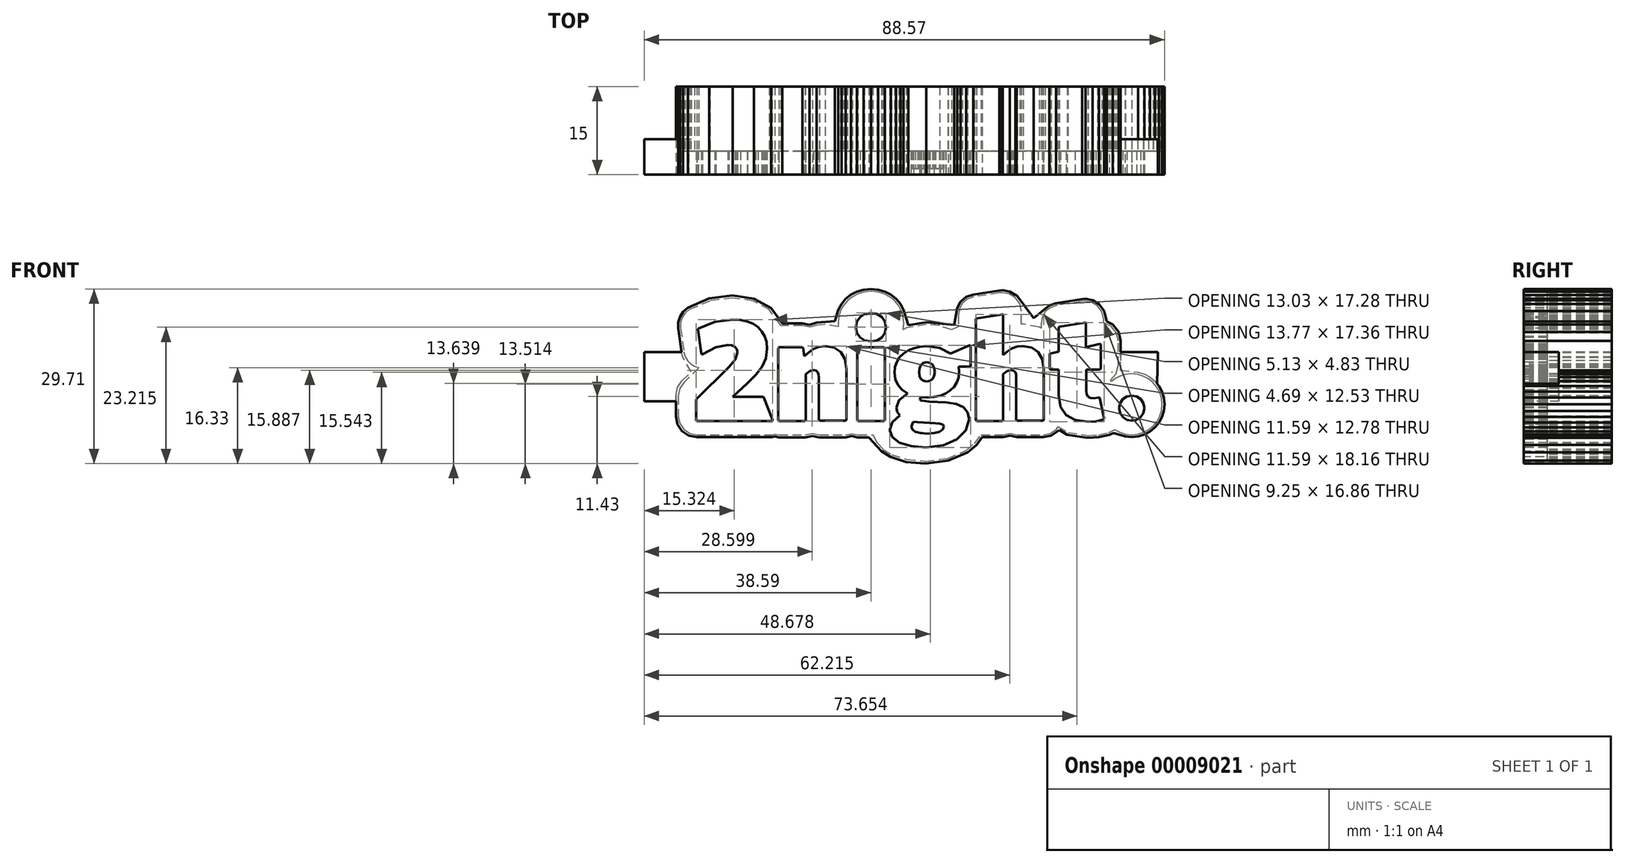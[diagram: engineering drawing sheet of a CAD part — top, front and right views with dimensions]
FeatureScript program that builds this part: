
annotation { "Feature Type Name" : "Feature", "Feature Type Description" : "" }
export const myFeature = defineFeature(function(context is Context, id is Id, definition is map)
    precondition{}
    {
        {
            var Q0;
            Q0=qCreatedBy(makeId("Front.planeOp"),FACE);
            var sketch = newSketch(context, id + "F0", { "sketchPlane" : qUnion([Q0])});
            skLineSegment(sketch, "E0", {"start": v(-31.92, 14.02) * mm, "end": v(-35.81, 13.52) * mm});
            skLineSegment(sketch, "E1", {"start": v(-35.81, 13.52) * mm, "end": v(-39.34, 12) * mm});
            skLineSegment(sketch, "E2", {"start": v(-39.34, 12) * mm, "end": v(-40.05, 11.41) * mm});
            skLineSegment(sketch, "E3", {"start": v(-40.05, 11.41) * mm, "end": v(-40.55, 10.66) * mm});
            skLineSegment(sketch, "E4", {"start": v(-40.55, 10.66) * mm, "end": v(-40.8, 9.8) * mm});
            skLineSegment(sketch, "E5", {"start": v(-40.8, 9.8) * mm, "end": v(-40.8, 8.88) * mm});
            skLineSegment(sketch, "E6", {"start": v(-40.8, 8.88) * mm, "end": v(-40.22, 4.8) * mm});
            skLineSegment(sketch, "E7", {"start": v(-40.22, 4.8) * mm, "end": v(-40.22, 4.75) * mm});
            skLineSegment(sketch, "E8", {"start": v(-40.22, 4.75) * mm, "end": v(-40, 4) * mm});
            skLineSegment(sketch, "E9", {"start": v(-40, 4) * mm, "end": v(-39.61, 3.32) * mm});
            skLineSegment(sketch, "E10", {"start": v(-39.61, 3.32) * mm, "end": v(-39.07, 2.76) * mm});
            skLineSegment(sketch, "E11", {"start": v(-39.07, 2.76) * mm, "end": v(-38.4, 2.35) * mm});
            skLineSegment(sketch, "E12", {"start": v(-38.4, 2.35) * mm, "end": v(-37.68, 2.13) * mm});
            skLineSegment(sketch, "E13", {"start": v(-37.68, 2.13) * mm, "end": v(-40.25, -0.38) * mm});
            skLineSegment(sketch, "E14", {"start": v(-40.25, -0.38) * mm, "end": v(-40.95, -1.42) * mm});
            skLineSegment(sketch, "E15", {"start": v(-40.95, -1.42) * mm, "end": v(-41.19, -2.65) * mm});
            skLineSegment(sketch, "E16", {"start": v(-41.19, -2.65) * mm, "end": v(-41.19, -6.12) * mm});
            skLineSegment(sketch, "E17", {"start": v(-41.19, -6.12) * mm, "end": v(-40.94, -7.35) * mm});
            skLineSegment(sketch, "E18", {"start": v(-40.94, -7.35) * mm, "end": v(-40.26, -8.36) * mm});
            skLineSegment(sketch, "E19", {"start": v(-40.26, -8.36) * mm, "end": v(-39.25, -9.04) * mm});
            skLineSegment(sketch, "E20", {"start": v(-39.25, -9.04) * mm, "end": v(-38.01, -9.3) * mm});
            skLineSegment(sketch, "E21", {"start": v(-38.01, -9.3) * mm, "end": v(-25.24, -9.3) * mm});
            skLineSegment(sketch, "E22", {"start": v(-25.24, -9.3) * mm, "end": v(-23.8, -8.94) * mm});
            skLineSegment(sketch, "E23", {"start": v(-23.8, -8.94) * mm, "end": v(-22.65, -7.97) * mm});
            skLineSegment(sketch, "E24", {"start": v(-22.65, -7.97) * mm, "end": v(-22.65, -7.92) * mm});
            skLineSegment(sketch, "E25", {"start": v(-22.65, -7.92) * mm, "end": v(-22.12, -6.5) * mm});
            skLineSegment(sketch, "E26", {"start": v(-22.12, -6.5) * mm, "end": v(-22.32, -5) * mm});
            skLineSegment(sketch, "E27", {"start": v(-22.32, -5) * mm, "end": v(-23.8, -1.16) * mm});
            skLineSegment(sketch, "E28", {"start": v(-23.8, -1.16) * mm, "end": v(-24.31, -0.3) * mm});
            skLineSegment(sketch, "E29", {"start": v(-24.31, -0.3) * mm, "end": v(-25.05, 0.36) * mm});
            skLineSegment(sketch, "E30", {"start": v(-25.05, 0.36) * mm, "end": v(-24.26, 1.54) * mm});
            skLineSegment(sketch, "E31", {"start": v(-24.26, 1.54) * mm, "end": v(-23.63, 2.87) * mm});
            skLineSegment(sketch, "E32", {"start": v(-23.63, 2.87) * mm, "end": v(-23.21, 4.36) * mm});
            skLineSegment(sketch, "E33", {"start": v(-23.21, 4.36) * mm, "end": v(-23.06, 6.04) * mm});
            skLineSegment(sketch, "E34", {"start": v(-23.06, 6.04) * mm, "end": v(-23.74, 9.38) * mm});
            skLineSegment(sketch, "E35", {"start": v(-23.74, 9.38) * mm, "end": v(-25.68, 12) * mm});
            skLineSegment(sketch, "E36", {"start": v(-25.68, 12) * mm, "end": v(-28.44, 13.5) * mm});
            skLineSegment(sketch, "E37", {"start": v(-28.44, 13.5) * mm, "end": v(-31.92, 14.02) * mm});
            skLineSegment(sketch, "E38", {"start": v(-16.2, 9.52) * mm, "end": v(-17.59, 9.39) * mm});
            skLineSegment(sketch, "E39", {"start": v(-17.59, 9.39) * mm, "end": v(-18.81, 9.02) * mm});
            skLineSegment(sketch, "E40", {"start": v(-18.81, 9.02) * mm, "end": v(-20.08, 9.27) * mm});
            skLineSegment(sketch, "E41", {"start": v(-20.08, 9.27) * mm, "end": v(-24.03, 9.27) * mm});
            skLineSegment(sketch, "E42", {"start": v(-24.03, 9.27) * mm, "end": v(-25.26, 9.02) * mm});
            skLineSegment(sketch, "E43", {"start": v(-25.26, 9.02) * mm, "end": v(-26.27, 8.35) * mm});
            skLineSegment(sketch, "E44", {"start": v(-26.27, 8.35) * mm, "end": v(-26.95, 7.34) * mm});
            skLineSegment(sketch, "E45", {"start": v(-26.95, 7.34) * mm, "end": v(-27.2, 6.1) * mm});
            skLineSegment(sketch, "E46", {"start": v(-27.2, 6.1) * mm, "end": v(-27.2, -6.15) * mm});
            skLineSegment(sketch, "E47", {"start": v(-27.2, -6.15) * mm, "end": v(-26.95, -7.38) * mm});
            skLineSegment(sketch, "E48", {"start": v(-26.95, -7.38) * mm, "end": v(-26.28, -8.39) * mm});
            skLineSegment(sketch, "E49", {"start": v(-26.28, -8.39) * mm, "end": v(-25.27, -9.07) * mm});
            skLineSegment(sketch, "E50", {"start": v(-25.27, -9.07) * mm, "end": v(-24.03, -9.32) * mm});
            skLineSegment(sketch, "E51", {"start": v(-24.03, -9.32) * mm, "end": v(-19.61, -9.32) * mm});
            skLineSegment(sketch, "E52", {"start": v(-19.61, -9.32) * mm, "end": v(-18.37, -9.07) * mm});
            skLineSegment(sketch, "E53", {"start": v(-18.37, -9.07) * mm, "end": v(-17.13, -9.32) * mm});
            skLineSegment(sketch, "E54", {"start": v(-17.13, -9.32) * mm, "end": v(-12.72, -9.32) * mm});
            skLineSegment(sketch, "E55", {"start": v(-12.72, -9.32) * mm, "end": v(-11.49, -9.07) * mm});
            skLineSegment(sketch, "E56", {"start": v(-11.49, -9.07) * mm, "end": v(-10.48, -8.4) * mm});
            skLineSegment(sketch, "E57", {"start": v(-10.48, -8.4) * mm, "end": v(-9.8, -7.39) * mm});
            skLineSegment(sketch, "E58", {"start": v(-9.8, -7.39) * mm, "end": v(-9.55, -6.15) * mm});
            skLineSegment(sketch, "E59", {"start": v(-9.55, -6.15) * mm, "end": v(-9.55, 2.49) * mm});
            skLineSegment(sketch, "E60", {"start": v(-9.55, 2.49) * mm, "end": v(-10.03, 5.39) * mm});
            skLineSegment(sketch, "E61", {"start": v(-10.03, 5.39) * mm, "end": v(-11.37, 7.6) * mm});
            skLineSegment(sketch, "E62", {"start": v(-11.37, 7.6) * mm, "end": v(-13.46, 9.02) * mm});
            skLineSegment(sketch, "E63", {"start": v(-13.46, 9.02) * mm, "end": v(-16.2, 9.52) * mm});
            skLineSegment(sketch, "E64", {"start": v(-8.39, 15.12) * mm, "end": v(-9.55, 15.01) * mm});
            skLineSegment(sketch, "E65", {"start": v(-9.55, 15.01) * mm, "end": v(-10.61, 14.7) * mm});
            skLineSegment(sketch, "E66", {"start": v(-10.61, 14.7) * mm, "end": v(-11.57, 14.21) * mm});
            skLineSegment(sketch, "E67", {"start": v(-11.57, 14.21) * mm, "end": v(-12.39, 13.56) * mm});
            skLineSegment(sketch, "E68", {"start": v(-12.39, 13.56) * mm, "end": v(-13.06, 12.76) * mm});
            skLineSegment(sketch, "E69", {"start": v(-13.06, 12.76) * mm, "end": v(-13.56, 11.83) * mm});
            skLineSegment(sketch, "E70", {"start": v(-13.56, 11.83) * mm, "end": v(-13.88, 10.79) * mm});
            skLineSegment(sketch, "E71", {"start": v(-13.88, 10.79) * mm, "end": v(-13.99, 9.66) * mm});
            skLineSegment(sketch, "E72", {"start": v(-13.99, 9.66) * mm, "end": v(-13.88, 8.54) * mm});
            skLineSegment(sketch, "E73", {"start": v(-13.88, 8.54) * mm, "end": v(-13.56, 7.5) * mm});
            skLineSegment(sketch, "E74", {"start": v(-13.56, 7.5) * mm, "end": v(-13.06, 6.58) * mm});
            skLineSegment(sketch, "E75", {"start": v(-13.06, 6.58) * mm, "end": v(-12.39, 5.78) * mm});
            skLineSegment(sketch, "E76", {"start": v(-12.39, 5.78) * mm, "end": v(-11.57, 5.13) * mm});
            skLineSegment(sketch, "E77", {"start": v(-11.57, 5.13) * mm, "end": v(-10.61, 4.64) * mm});
            skLineSegment(sketch, "E78", {"start": v(-10.61, 4.64) * mm, "end": v(-9.55, 4.33) * mm});
            skLineSegment(sketch, "E79", {"start": v(-9.55, 4.33) * mm, "end": v(-8.39, 4.22) * mm});
            skLineSegment(sketch, "E80", {"start": v(-8.39, 4.22) * mm, "end": v(-7.23, 4.33) * mm});
            skLineSegment(sketch, "E81", {"start": v(-7.23, 4.33) * mm, "end": v(-6.16, 4.64) * mm});
            skLineSegment(sketch, "E82", {"start": v(-6.16, 4.64) * mm, "end": v(-5.2, 5.13) * mm});
            skLineSegment(sketch, "E83", {"start": v(-5.2, 5.13) * mm, "end": v(-4.39, 5.78) * mm});
            skLineSegment(sketch, "E84", {"start": v(-4.39, 5.78) * mm, "end": v(-3.71, 6.58) * mm});
            skLineSegment(sketch, "E85", {"start": v(-3.71, 6.58) * mm, "end": v(-3.21, 7.5) * mm});
            skLineSegment(sketch, "E86", {"start": v(-3.21, 7.5) * mm, "end": v(-2.9, 8.54) * mm});
            skLineSegment(sketch, "E87", {"start": v(-2.9, 8.54) * mm, "end": v(-2.79, 9.66) * mm});
            skLineSegment(sketch, "E88", {"start": v(-2.79, 9.66) * mm, "end": v(-2.89, 10.79) * mm});
            skLineSegment(sketch, "E89", {"start": v(-2.89, 10.79) * mm, "end": v(-3.2, 11.83) * mm});
            skLineSegment(sketch, "E90", {"start": v(-3.2, 11.83) * mm, "end": v(-3.7, 12.76) * mm});
            skLineSegment(sketch, "E91", {"start": v(-3.7, 12.76) * mm, "end": v(-4.38, 13.56) * mm});
            skLineSegment(sketch, "E92", {"start": v(-4.38, 13.56) * mm, "end": v(-5.2, 14.21) * mm});
            skLineSegment(sketch, "E93", {"start": v(-5.2, 14.21) * mm, "end": v(-6.16, 14.7) * mm});
            skLineSegment(sketch, "E94", {"start": v(-6.16, 14.7) * mm, "end": v(-7.23, 15.01) * mm});
            skLineSegment(sketch, "E95", {"start": v(-7.23, 15.01) * mm, "end": v(-8.39, 15.12) * mm});
            skLineSegment(sketch, "E96", {"start": v(-6.18, 9.27) * mm, "end": v(-10.6, 9.27) * mm});
            skLineSegment(sketch, "E97", {"start": v(-10.6, 9.27) * mm, "end": v(-11.82, 9.02) * mm});
            skLineSegment(sketch, "E98", {"start": v(-11.82, 9.02) * mm, "end": v(-12.83, 8.35) * mm});
            skLineSegment(sketch, "E99", {"start": v(-12.83, 8.35) * mm, "end": v(-13.52, 7.34) * mm});
            skLineSegment(sketch, "E100", {"start": v(-13.52, 7.34) * mm, "end": v(-13.77, 6.1) * mm});
            skLineSegment(sketch, "E101", {"start": v(-13.77, 6.1) * mm, "end": v(-13.77, -6.15) * mm});
            skLineSegment(sketch, "E102", {"start": v(-13.77, -6.15) * mm, "end": v(-13.52, -7.38) * mm});
            skLineSegment(sketch, "E103", {"start": v(-13.52, -7.38) * mm, "end": v(-12.84, -8.39) * mm});
            skLineSegment(sketch, "E104", {"start": v(-12.84, -8.39) * mm, "end": v(-11.83, -9.07) * mm});
            skLineSegment(sketch, "E105", {"start": v(-11.83, -9.07) * mm, "end": v(-10.6, -9.32) * mm});
            skLineSegment(sketch, "E106", {"start": v(-10.6, -9.32) * mm, "end": v(-6.18, -9.32) * mm});
            skLineSegment(sketch, "E107", {"start": v(-6.18, -9.32) * mm, "end": v(-4.95, -9.07) * mm});
            skLineSegment(sketch, "E108", {"start": v(-4.95, -9.07) * mm, "end": v(-3.94, -8.4) * mm});
            skLineSegment(sketch, "E109", {"start": v(-3.94, -8.4) * mm, "end": v(-3.26, -7.39) * mm});
            skLineSegment(sketch, "E110", {"start": v(-3.26, -7.39) * mm, "end": v(-3, -6.15) * mm});
            skLineSegment(sketch, "E111", {"start": v(-3, -6.15) * mm, "end": v(-3, 6.13) * mm});
            skLineSegment(sketch, "E112", {"start": v(-3, 6.13) * mm, "end": v(-3.26, 7.35) * mm});
            skLineSegment(sketch, "E113", {"start": v(-3.26, 7.35) * mm, "end": v(-3.94, 8.35) * mm});
            skLineSegment(sketch, "E114", {"start": v(-3.94, 8.35) * mm, "end": v(-4.95, 9.03) * mm});
            skLineSegment(sketch, "E115", {"start": v(-4.95, 9.03) * mm, "end": v(-6.18, 9.27) * mm});
            skLineSegment(sketch, "E116", {"start": v(8.39, 9.63) * mm, "end": v(7.17, 9.38) * mm});
            skLineSegment(sketch, "E117", {"start": v(7.17, 9.38) * mm, "end": v(5.32, 8.6) * mm});
            skLineSegment(sketch, "E118", {"start": v(5.32, 8.6) * mm, "end": v(3.3, 9.27) * mm});
            skLineSegment(sketch, "E119", {"start": v(3.3, 9.27) * mm, "end": v(1.05, 9.5) * mm});
            skLineSegment(sketch, "E120", {"start": v(1.05, 9.5) * mm, "end": v(-2.35, 8.93) * mm});
            skLineSegment(sketch, "E121", {"start": v(-2.35, 8.93) * mm, "end": v(-5.04, 7.36) * mm});
            skLineSegment(sketch, "E122", {"start": v(-5.04, 7.36) * mm, "end": v(-6.81, 4.97) * mm});
            skLineSegment(sketch, "E123", {"start": v(-6.81, 4.97) * mm, "end": v(-7.45, 1.93) * mm});
            skLineSegment(sketch, "E124", {"start": v(-7.45, 1.93) * mm, "end": v(-7.2, 0.06) * mm});
            skLineSegment(sketch, "E125", {"start": v(-7.2, 0.06) * mm, "end": v(-6.51, -1.6) * mm});
            skLineSegment(sketch, "E126", {"start": v(-6.51, -1.6) * mm, "end": v(-7, -2.85) * mm});
            skLineSegment(sketch, "E127", {"start": v(-7, -2.85) * mm, "end": v(-7.14, -3.97) * mm});
            skLineSegment(sketch, "E128", {"start": v(-7.14, -3.97) * mm, "end": v(-7.12, -4.44) * mm});
            skLineSegment(sketch, "E129", {"start": v(-7.12, -4.44) * mm, "end": v(-7.99, -6) * mm});
            skLineSegment(sketch, "E130", {"start": v(-7.99, -6) * mm, "end": v(-8.28, -7.8) * mm});
            skLineSegment(sketch, "E131", {"start": v(-8.28, -7.8) * mm, "end": v(-8.05, -9.3) * mm});
            skLineSegment(sketch, "E132", {"start": v(-8.05, -9.3) * mm, "end": v(-7.39, -10.63) * mm});
            skLineSegment(sketch, "E133", {"start": v(-7.39, -10.63) * mm, "end": v(-6.32, -11.77) * mm});
            skLineSegment(sketch, "E134", {"start": v(-6.32, -11.77) * mm, "end": v(-4.88, -12.69) * mm});
            skLineSegment(sketch, "E135", {"start": v(-4.88, -12.69) * mm, "end": v(-2.3, -13.52) * mm});
            skLineSegment(sketch, "E136", {"start": v(-2.3, -13.52) * mm, "end": v(0.88, -13.8) * mm});
            skLineSegment(sketch, "E137", {"start": v(0.88, -13.8) * mm, "end": v(4.69, -13.32) * mm});
            skLineSegment(sketch, "E138", {"start": v(4.69, -13.32) * mm, "end": v(7.83, -11.94) * mm});
            skLineSegment(sketch, "E139", {"start": v(7.83, -11.94) * mm, "end": v(9.29, -10.73) * mm});
            skLineSegment(sketch, "E140", {"start": v(9.29, -10.73) * mm, "end": v(10.36, -9.3) * mm});
            skLineSegment(sketch, "E141", {"start": v(10.36, -9.3) * mm, "end": v(11.03, -7.68) * mm});
            skLineSegment(sketch, "E142", {"start": v(11.03, -7.68) * mm, "end": v(11.25, -5.93) * mm});
            skLineSegment(sketch, "E143", {"start": v(11.25, -5.93) * mm, "end": v(11.17, -4.91) * mm});
            skLineSegment(sketch, "E144", {"start": v(11.17, -4.91) * mm, "end": v(10.83, -3.68) * mm});
            skLineSegment(sketch, "E145", {"start": v(10.83, -3.68) * mm, "end": v(10.07, -2.4) * mm});
            skLineSegment(sketch, "E146", {"start": v(10.07, -2.4) * mm, "end": v(8.74, -1.24) * mm});
            skLineSegment(sketch, "E147", {"start": v(8.74, -1.24) * mm, "end": v(9.3, 0.14) * mm});
            skLineSegment(sketch, "E148", {"start": v(9.3, 0.14) * mm, "end": v(10.6, 0.91) * mm});
            skLineSegment(sketch, "E149", {"start": v(10.6, 0.91) * mm, "end": v(10.65, 0.97) * mm});
            skLineSegment(sketch, "E150", {"start": v(10.65, 0.97) * mm, "end": v(11.3, 1.98) * mm});
            skLineSegment(sketch, "E151", {"start": v(11.3, 1.98) * mm, "end": v(11.53, 3.15) * mm});
            skLineSegment(sketch, "E152", {"start": v(11.53, 3.15) * mm, "end": v(11.5, 6.49) * mm});
            skLineSegment(sketch, "E153", {"start": v(11.5, 6.49) * mm, "end": v(11.13, 7.96) * mm});
            skLineSegment(sketch, "E154", {"start": v(11.13, 7.96) * mm, "end": v(10.12, 9.08) * mm});
            skLineSegment(sketch, "E155", {"start": v(10.12, 9.08) * mm, "end": v(9.3, 9.49) * mm});
            skLineSegment(sketch, "E156", {"start": v(9.3, 9.49) * mm, "end": v(8.39, 9.63) * mm});
            skLineSegment(sketch, "E157", {"start": v(14.01, 14.9) * mm, "end": v(13.63, 14.87) * mm});
            skLineSegment(sketch, "E158", {"start": v(13.63, 14.87) * mm, "end": v(13.52, 14.87) * mm});
            skLineSegment(sketch, "E159", {"start": v(13.52, 14.87) * mm, "end": v(9.1, 14.18) * mm});
            skLineSegment(sketch, "E160", {"start": v(9.1, 14.18) * mm, "end": v(8.04, 13.8) * mm});
            skLineSegment(sketch, "E161", {"start": v(8.04, 13.8) * mm, "end": v(7.2, 13.11) * mm});
            skLineSegment(sketch, "E162", {"start": v(7.2, 13.11) * mm, "end": v(6.65, 12.17) * mm});
            skLineSegment(sketch, "E163", {"start": v(6.65, 12.17) * mm, "end": v(6.45, 11.06) * mm});
            skLineSegment(sketch, "E164", {"start": v(6.45, 11.06) * mm, "end": v(6.45, -6.12) * mm});
            skLineSegment(sketch, "E165", {"start": v(6.45, -6.12) * mm, "end": v(6.7, -7.35) * mm});
            skLineSegment(sketch, "E166", {"start": v(6.7, -7.35) * mm, "end": v(7.38, -8.36) * mm});
            skLineSegment(sketch, "E167", {"start": v(7.38, -8.36) * mm, "end": v(8.39, -9.04) * mm});
            skLineSegment(sketch, "E168", {"start": v(8.39, -9.04) * mm, "end": v(9.63, -9.3) * mm});
            skLineSegment(sketch, "E169", {"start": v(9.63, -9.3) * mm, "end": v(14.04, -9.3) * mm});
            skLineSegment(sketch, "E170", {"start": v(14.04, -9.3) * mm, "end": v(15.28, -9.05) * mm});
            skLineSegment(sketch, "E171", {"start": v(15.28, -9.05) * mm, "end": v(16.52, -9.3) * mm});
            skLineSegment(sketch, "E172", {"start": v(16.52, -9.3) * mm, "end": v(20.94, -9.3) * mm});
            skLineSegment(sketch, "E173", {"start": v(20.94, -9.3) * mm, "end": v(22.17, -9.05) * mm});
            skLineSegment(sketch, "E174", {"start": v(22.17, -9.05) * mm, "end": v(23.17, -8.37) * mm});
            skLineSegment(sketch, "E175", {"start": v(23.17, -8.37) * mm, "end": v(23.86, -7.36) * mm});
            skLineSegment(sketch, "E176", {"start": v(23.86, -7.36) * mm, "end": v(24.1, -6.12) * mm});
            skLineSegment(sketch, "E177", {"start": v(24.1, -6.12) * mm, "end": v(24.1, 2.51) * mm});
            skLineSegment(sketch, "E178", {"start": v(24.1, 2.51) * mm, "end": v(23.64, 5.42) * mm});
            skLineSegment(sketch, "E179", {"start": v(23.64, 5.42) * mm, "end": v(22.31, 7.63) * mm});
            skLineSegment(sketch, "E180", {"start": v(22.31, 7.63) * mm, "end": v(20.23, 9.05) * mm});
            skLineSegment(sketch, "E181", {"start": v(20.23, 9.05) * mm, "end": v(17.52, 9.55) * mm});
            skLineSegment(sketch, "E182", {"start": v(17.52, 9.55) * mm, "end": v(17.24, 9.55) * mm});
            skLineSegment(sketch, "E183", {"start": v(17.24, 9.55) * mm, "end": v(17.24, 11.75) * mm});
            skLineSegment(sketch, "E184", {"start": v(17.24, 11.75) * mm, "end": v(16.96, 13.05) * mm});
            skLineSegment(sketch, "E185", {"start": v(16.96, 13.05) * mm, "end": v(16.17, 14.13) * mm});
            skLineSegment(sketch, "E186", {"start": v(16.17, 14.13) * mm, "end": v(16.08, 14.13) * mm});
            skLineSegment(sketch, "E187", {"start": v(16.08, 14.13) * mm, "end": v(16.06, 14.15) * mm});
            skLineSegment(sketch, "E188", {"start": v(16.06, 14.15) * mm, "end": v(15.1, 14.7) * mm});
            skLineSegment(sketch, "E189", {"start": v(15.1, 14.7) * mm, "end": v(14.01, 14.9) * mm});
            skLineSegment(sketch, "E190", {"start": v(28.08, 13.46) * mm, "end": v(27.59, 13.44) * mm});
            skLineSegment(sketch, "E191", {"start": v(27.59, 13.44) * mm, "end": v(23.23, 12.75) * mm});
            skLineSegment(sketch, "E192", {"start": v(23.23, 12.75) * mm, "end": v(22.16, 12.38) * mm});
            skLineSegment(sketch, "E193", {"start": v(22.16, 12.38) * mm, "end": v(21.3, 11.68) * mm});
            skLineSegment(sketch, "E194", {"start": v(21.3, 11.68) * mm, "end": v(20.75, 10.75) * mm});
            skLineSegment(sketch, "E195", {"start": v(20.75, 10.75) * mm, "end": v(20.55, 9.63) * mm});
            skLineSegment(sketch, "E196", {"start": v(20.55, 9.63) * mm, "end": v(20.55, 7.78) * mm});
            skLineSegment(sketch, "E197", {"start": v(20.55, 7.78) * mm, "end": v(19.91, 7.29) * mm});
            skLineSegment(sketch, "E198", {"start": v(19.91, 7.29) * mm, "end": v(19.43, 6.65) * mm});
            skLineSegment(sketch, "E199", {"start": v(19.43, 6.65) * mm, "end": v(19.12, 5.9) * mm});
            skLineSegment(sketch, "E200", {"start": v(19.12, 5.9) * mm, "end": v(19, 5.08) * mm});
            skLineSegment(sketch, "E201", {"start": v(19, 5.08) * mm, "end": v(19, 2.6) * mm});
            skLineSegment(sketch, "E202", {"start": v(19, 2.6) * mm, "end": v(19.12, 1.76) * mm});
            skLineSegment(sketch, "E203", {"start": v(19.12, 1.76) * mm, "end": v(19.43, 1.02) * mm});
            skLineSegment(sketch, "E204", {"start": v(19.43, 1.02) * mm, "end": v(19.91, 0.38) * mm});
            skLineSegment(sketch, "E205", {"start": v(19.91, 0.38) * mm, "end": v(20.55, -0.1) * mm});
            skLineSegment(sketch, "E206", {"start": v(20.55, -0.1) * mm, "end": v(20.55, -1.85) * mm});
            skLineSegment(sketch, "E207", {"start": v(20.55, -1.85) * mm, "end": v(21.1, -5.03) * mm});
            skLineSegment(sketch, "E208", {"start": v(21.1, -5.03) * mm, "end": v(22.67, -7.42) * mm});
            skLineSegment(sketch, "E209", {"start": v(22.67, -7.42) * mm, "end": v(25.18, -8.91) * mm});
            skLineSegment(sketch, "E210", {"start": v(25.18, -8.91) * mm, "end": v(28.55, -9.43) * mm});
            skLineSegment(sketch, "E211", {"start": v(28.55, -9.43) * mm, "end": v(30.34, -9.32) * mm});
            skLineSegment(sketch, "E212", {"start": v(30.34, -9.32) * mm, "end": v(32.06, -8.94) * mm});
            skLineSegment(sketch, "E213", {"start": v(32.06, -8.94) * mm, "end": v(33.1, -8.39) * mm});
            skLineSegment(sketch, "E214", {"start": v(33.1, -8.39) * mm, "end": v(33.87, -7.51) * mm});
            skLineSegment(sketch, "E215", {"start": v(33.87, -7.51) * mm, "end": v(34.27, -6.43) * mm});
            skLineSegment(sketch, "E216", {"start": v(34.27, -6.43) * mm, "end": v(34.24, -5.24) * mm});
            skLineSegment(sketch, "E217", {"start": v(34.24, -5.24) * mm, "end": v(33.46, -1.74) * mm});
            skLineSegment(sketch, "E218", {"start": v(33.46, -1.74) * mm, "end": v(33.07, -0.77) * mm});
            skLineSegment(sketch, "E219", {"start": v(33.07, -0.77) * mm, "end": v(32.39, 0) * mm});
            skLineSegment(sketch, "E220", {"start": v(32.39, 0) * mm, "end": v(33.35, 1.1) * mm});
            skLineSegment(sketch, "E221", {"start": v(33.35, 1.1) * mm, "end": v(33.71, 2.54) * mm});
            skLineSegment(sketch, "E222", {"start": v(33.71, 2.54) * mm, "end": v(33.74, 6.68) * mm});
            skLineSegment(sketch, "E223", {"start": v(33.74, 6.68) * mm, "end": v(33.42, 8.05) * mm});
            skLineSegment(sketch, "E224", {"start": v(33.42, 8.05) * mm, "end": v(32.52, 9.16) * mm});
            skLineSegment(sketch, "E225", {"start": v(32.52, 9.16) * mm, "end": v(31.26, 9.77) * mm});
            skLineSegment(sketch, "E226", {"start": v(31.26, 9.77) * mm, "end": v(31.26, 10.3) * mm});
            skLineSegment(sketch, "E227", {"start": v(31.26, 10.3) * mm, "end": v(30.96, 11.63) * mm});
            skLineSegment(sketch, "E228", {"start": v(30.96, 11.63) * mm, "end": v(30.15, 12.7) * mm});
            skLineSegment(sketch, "E229", {"start": v(30.15, 12.7) * mm, "end": v(29.19, 13.26) * mm});
            skLineSegment(sketch, "E230", {"start": v(29.19, 13.26) * mm, "end": v(28.08, 13.46) * mm});
            skLineSegment(sketch, "E231", {"start": v(36, 1.08) * mm, "end": v(34.95, 0.97) * mm});
            skLineSegment(sketch, "E232", {"start": v(34.95, 0.97) * mm, "end": v(33.98, 0.67) * mm});
            skLineSegment(sketch, "E233", {"start": v(33.98, 0.67) * mm, "end": v(33.1, 0.2) * mm});
            skLineSegment(sketch, "E234", {"start": v(33.1, 0.2) * mm, "end": v(32.33, -0.44) * mm});
            skLineSegment(sketch, "E235", {"start": v(32.33, -0.44) * mm, "end": v(31.7, -1.2) * mm});
            skLineSegment(sketch, "E236", {"start": v(31.7, -1.2) * mm, "end": v(31.22, -2.09) * mm});
            skLineSegment(sketch, "E237", {"start": v(31.22, -2.09) * mm, "end": v(30.92, -3.06) * mm});
            skLineSegment(sketch, "E238", {"start": v(30.92, -3.06) * mm, "end": v(30.81, -4.1) * mm});
            skLineSegment(sketch, "E239", {"start": v(30.81, -4.1) * mm, "end": v(30.92, -5.15) * mm});
            skLineSegment(sketch, "E240", {"start": v(30.92, -5.15) * mm, "end": v(31.22, -6.13) * mm});
            skLineSegment(sketch, "E241", {"start": v(31.22, -6.13) * mm, "end": v(31.7, -7) * mm});
            skLineSegment(sketch, "E242", {"start": v(31.7, -7) * mm, "end": v(32.33, -7.78) * mm});
            skLineSegment(sketch, "E243", {"start": v(32.33, -7.78) * mm, "end": v(33.1, -8.4) * mm});
            skLineSegment(sketch, "E244", {"start": v(33.1, -8.4) * mm, "end": v(33.98, -8.89) * mm});
            skLineSegment(sketch, "E245", {"start": v(33.98, -8.89) * mm, "end": v(34.95, -9.19) * mm});
            skLineSegment(sketch, "E246", {"start": v(34.95, -9.19) * mm, "end": v(36, -9.3) * mm});
            skLineSegment(sketch, "E247", {"start": v(36, -9.3) * mm, "end": v(37.05, -9.19) * mm});
            skLineSegment(sketch, "E248", {"start": v(37.05, -9.19) * mm, "end": v(38.02, -8.89) * mm});
            skLineSegment(sketch, "E249", {"start": v(38.02, -8.89) * mm, "end": v(38.9, -8.4) * mm});
            skLineSegment(sketch, "E250", {"start": v(38.9, -8.4) * mm, "end": v(39.67, -7.78) * mm});
            skLineSegment(sketch, "E251", {"start": v(39.67, -7.78) * mm, "end": v(40.3, -7) * mm});
            skLineSegment(sketch, "E252", {"start": v(40.3, -7) * mm, "end": v(40.78, -6.13) * mm});
            skLineSegment(sketch, "E253", {"start": v(40.78, -6.13) * mm, "end": v(41.08, -5.15) * mm});
            skLineSegment(sketch, "E254", {"start": v(41.08, -5.15) * mm, "end": v(41.19, -4.1) * mm});
            skLineSegment(sketch, "E255", {"start": v(41.19, -4.1) * mm, "end": v(41.08, -3.06) * mm});
            skLineSegment(sketch, "E256", {"start": v(41.08, -3.06) * mm, "end": v(40.78, -2.09) * mm});
            skLineSegment(sketch, "E257", {"start": v(40.78, -2.09) * mm, "end": v(40.3, -1.2) * mm});
            skLineSegment(sketch, "E258", {"start": v(40.3, -1.2) * mm, "end": v(39.66, -0.44) * mm});
            skLineSegment(sketch, "E259", {"start": v(39.66, -0.44) * mm, "end": v(38.89, 0.2) * mm});
            skLineSegment(sketch, "E260", {"start": v(38.89, 0.2) * mm, "end": v(38, 0.67) * mm});
            skLineSegment(sketch, "E261", {"start": v(38, 0.67) * mm, "end": v(37.04, 0.97) * mm});
            skLineSegment(sketch, "E262", {"start": v(37.04, 0.97) * mm, "end": v(36, 1.08) * mm});
            skSolve(sketch);
        }
        {
            var Q0;
            {var subQ12=sQuery(id+"F0.wireOp",EDGE,"E86");Q0=makeQuery(id+"F0.imprint","IMPRINT",FACE,{"disambiguationData":[TD([[makeQuery(id+"F0.imprint","IMPRINT",EDGE,{"derivedFrom":subQ12}),-1.0]])]});}
            var Q1;
            Q1=makeQuery(id+"F0.imprint","IMPRINT",FACE,{"disambiguationData":[TD([[makeQuery(id+"F0.imprint","IMPRINT",EDGE,{"derivedFrom":sQuery(id+"F0.wireOp",EDGE,"E0")}),1.0]])]});
            var Q2;
            {var subQ3=sQuery(id+"F0.wireOp",EDGE,"E214");Q2=makeQuery(id+"F0.imprint","IMPRINT",FACE,{"disambiguationData":[TD([[makeQuery(id+"F0.imprint","IMPRINT",EDGE,{"derivedFrom":subQ3}),-1.0]])]});}
            var Q3;
            {var subQ3=sQuery(id+"F0.wireOp",EDGE,"E23");Q3=makeQuery(id+"F0.imprint","IMPRINT",FACE,{"disambiguationData":[TD([[makeQuery(id+"F0.imprint","IMPRINT",EDGE,{"derivedFrom":subQ3}),1.0]])]});}
            var Q4;
            {var subQ9=sQuery(id+"F0.wireOp",EDGE,"E116");Q4=makeQuery(id+"F0.imprint","IMPRINT",FACE,{"disambiguationData":[TD([[makeQuery(id+"F0.imprint","IMPRINT",EDGE,{"derivedFrom":subQ9}),-1.0]])]});}
            var Q5;
            {var subQ4=sQuery(id+"F0.wireOp",EDGE,"E116");Q5=makeQuery(id+"F0.imprint","IMPRINT",FACE,{"disambiguationData":[TD([[makeQuery(id+"F0.imprint","IMPRINT",EDGE,{"derivedFrom":subQ4}),1.0]])]});}
            var Q6;
            {var subQ17=sQuery(id+"F0.wireOp",EDGE,"E176");Q6=makeQuery(id+"F0.imprint","IMPRINT",FACE,{"disambiguationData":[TD([[makeQuery(id+"F0.imprint","IMPRINT",EDGE,{"derivedFrom":subQ17}),-1.0]])]});}
            var Q7;
            {var subQ9=sQuery(id+"F0.wireOp",EDGE,"E176");Q7=makeQuery(id+"F0.imprint","IMPRINT",FACE,{"disambiguationData":[TD([[makeQuery(id+"F0.imprint","IMPRINT",EDGE,{"derivedFrom":subQ9}),1.0]])]});}
            var Q8;
            {var subQ17=sQuery(id+"F0.wireOp",EDGE,"E23");Q8=makeQuery(id+"F0.imprint","IMPRINT",FACE,{"disambiguationData":[TD([[makeQuery(id+"F0.imprint","IMPRINT",EDGE,{"derivedFrom":subQ17}),-1.0]])]});}
            var Q9;
            {var subQ14=sQuery(id+"F0.wireOp",EDGE,"E56");Q9=makeQuery(id+"F0.imprint","IMPRINT",FACE,{"disambiguationData":[TD([[makeQuery(id+"F0.imprint","IMPRINT",EDGE,{"derivedFrom":subQ14}),1.0]])]});}
            var Q10;
            {var subQ12=sQuery(id+"F0.wireOp",EDGE,"E82");Q10=makeQuery(id+"F0.imprint","IMPRINT",FACE,{"disambiguationData":[TD([[makeQuery(id+"F0.imprint","IMPRINT",EDGE,{"derivedFrom":subQ12}),-1.0]])]});}
            var Q11;
            {var subQ18=sQuery(id+"F0.wireOp",EDGE,"E56");Q11=makeQuery(id+"F0.imprint","IMPRINT",FACE,{"disambiguationData":[TD([[makeQuery(id+"F0.imprint","IMPRINT",EDGE,{"derivedFrom":subQ18}),-1.0]])]});}
            var Q12;
            {var subQ17=sQuery(id+"F0.wireOp",EDGE,"E61");Q12=makeQuery(id+"F0.imprint","IMPRINT",FACE,{"disambiguationData":[TD([[makeQuery(id+"F0.imprint","IMPRINT",EDGE,{"derivedFrom":subQ17}),-1.0]])]});}
            var Q13;
            {var subQ9=sQuery(id+"F0.wireOp",EDGE,"E214");Q13=makeQuery(id+"F0.imprint","IMPRINT",FACE,{"disambiguationData":[TD([[makeQuery(id+"F0.imprint","IMPRINT",EDGE,{"derivedFrom":subQ9}),1.0]])]});}
            var Q14;
            Q14=makeQuery(id+"F0.imprint","IMPRINT",FACE,{"disambiguationData":[TD([[makeQuery(id+"F0.imprint","IMPRINT",EDGE,{"derivedFrom":sQuery(id+"F0.wireOp",EDGE,"E64")}),1.0]])]});
            var Q15;
            {var subQ10=sQuery(id+"F0.wireOp",EDGE,"E82");Q15=makeQuery(id+"F0.imprint","IMPRINT",FACE,{"disambiguationData":[TD([[makeQuery(id+"F0.imprint","IMPRINT",EDGE,{"derivedFrom":subQ10}),1.0]])]});}
            var Q16;
            {var subQ12=sQuery(id+"F0.wireOp",EDGE,"E61");Q16=makeQuery(id+"F0.imprint","IMPRINT",FACE,{"disambiguationData":[TD([[makeQuery(id+"F0.imprint","IMPRINT",EDGE,{"derivedFrom":subQ12}),1.0]])]});}
            var Q17;
            {var subQ7=sQuery(id+"F0.wireOp",EDGE,"E86");Q17=makeQuery(id+"F0.imprint","IMPRINT",FACE,{"disambiguationData":[TD([[makeQuery(id+"F0.imprint","IMPRINT",EDGE,{"derivedFrom":subQ7}),1.0]])]});}
            var Q18;
            {var subQ7=sQuery(id+"F0.wireOp",EDGE,"E73");Q18=makeQuery(id+"F0.imprint","IMPRINT",FACE,{"disambiguationData":[TD([[makeQuery(id+"F0.imprint","IMPRINT",EDGE,{"derivedFrom":subQ7}),1.0]])]});}
            var Q19;
            Q19=sQuery(id+"F0.wireOp",EDGE,"E164");
            var Q20;
            Q20=sQuery(id+"F0.wireOp",EDGE,"E21");
            var Q21;
            Q21=sQuery(id+"F0.wireOp",EDGE,"E101");
            var Q22;
            Q22=sQuery(id+"F0.wireOp",EDGE,"E59");
            var Q23;
            Q23=sQuery(id+"F0.wireOp",EDGE,"E46");
            var Q24;
            Q24=sQuery(id+"F0.wireOp",EDGE,"E111");
            var Q25;
            Q25=sQuery(id+"F0.wireOp",EDGE,"E177");
            var Q26;
            Q26=sQuery(id+"F0.wireOp",EDGE,"E116");
            var Q27;
            Q27=sQuery(id+"F0.wireOp",EDGE,"E53");
            var Q28;
            Q28=sQuery(id+"F0.wireOp",EDGE,"E37");
            var Q29;
            Q29=sQuery(id+"F0.wireOp",EDGE,"E117");
            var Q30;
            Q30=sQuery(id+"F0.wireOp",EDGE,"E229");
            var Q31;
            Q31=sQuery(id+"F0.wireOp",EDGE,"E54");
            var Q32;
            Q32=sQuery(id+"F0.wireOp",EDGE,"E134");
            var Q33;
            Q33=sQuery(id+"F0.wireOp",EDGE,"E118");
            var Q34;
            Q34=sQuery(id+"F0.wireOp",EDGE,"E230");
            var Q35;
            Q35=sQuery(id+"F0.wireOp",EDGE,"E119");
            var Q36;
            Q36=sQuery(id+"F0.wireOp",EDGE,"E183");
            var Q37;
            Q37=sQuery(id+"F0.wireOp",EDGE,"E135");
            var Q38;
            Q38=sQuery(id+"F0.wireOp",EDGE,"E120");
            var Q39;
            Q39=sQuery(id+"F0.wireOp",EDGE,"E152");
            var Q40;
            Q40=sQuery(id+"F0.wireOp",EDGE,"E136");
            var Q41;
            Q41=sQuery(id+"F0.wireOp",EDGE,"E41");
            var Q42;
            Q42=sQuery(id+"F0.wireOp",EDGE,"E153");
            var Q43;
            Q43=sQuery(id+"F0.wireOp",EDGE,"E137");
            var Q44;
            Q44=sQuery(id+"F0.wireOp",EDGE,"E201");
            var Q45;
            Q45=sQuery(id+"F0.wireOp",EDGE,"E154");
            var Q46;
            Q46=sQuery(id+"F0.wireOp",EDGE,"E138");
            var Q47;
            Q47=sQuery(id+"F0.wireOp",EDGE,"E202");
            var Q48;
            Q48=sQuery(id+"F0.wireOp",EDGE,"E27");
            var Q49;
            Q49=sQuery(id+"F0.wireOp",EDGE,"E20");
            var Q50;
            Q50=sQuery(id+"F0.wireOp",EDGE,"E52");
            var Q51;
            Q51=sQuery(id+"F0.wireOp",EDGE,"E36");
            var Q52;
            Q52=sQuery(id+"F0.wireOp",EDGE,"E155");
            var Q53;
            Q53=sQuery(id+"F0.wireOp",EDGE,"E203");
            var Q54;
            Q54=sQuery(id+"F0.wireOp",EDGE,"E172");
            var Q55;
            Q55=sQuery(id+"F0.wireOp",EDGE,"E156");
            var Q56;
            Q56=sQuery(id+"F0.wireOp",EDGE,"E14");
            var Q57;
            Q57=sQuery(id+"F0.wireOp",EDGE,"E15");
            var Q58;
            Q58=sQuery(id+"F0.wireOp",EDGE,"E0");
            var Q59;
            Q59=sQuery(id+"F0.wireOp",EDGE,"E1");
            var Q60;
            Q60=sQuery(id+"F0.wireOp",EDGE,"E6");
            var Q61;
            Q61=sQuery(id+"F0.wireOp",EDGE,"E45");
            var Q62;
            Q62=sQuery(id+"F0.wireOp",EDGE,"E109");
            var Q63;
            Q63=sQuery(id+"F0.wireOp",EDGE,"E110");
            var Q64;
            Q64=sQuery(id+"F0.wireOp",EDGE,"E190");
            var Q65;
            Q65=sQuery(id+"F0.wireOp",EDGE,"E222");
            var Q66;
            Q66=sQuery(id+"F0.wireOp",EDGE,"E207");
            var Q67;
            Q67=sQuery(id+"F0.wireOp",EDGE,"E191");
            var Q68;
            Q68=sQuery(id+"F0.wireOp",EDGE,"E192");
            var Q69;
            Q69=sQuery(id+"F0.wireOp",EDGE,"E16");
            var Q70;
            Q70=sQuery(id+"F0.wireOp",EDGE,"E193");
            var Q71;
            Q71=sQuery(id+"F0.wireOp",EDGE,"E17");
            var Q72;
            Q72=sQuery(id+"F0.wireOp",EDGE,"E33");
            var Q73;
            Q73=sQuery(id+"F0.wireOp",EDGE,"E258");
            var Q74;
            Q74=sQuery(id+"F0.wireOp",EDGE,"E18");
            var Q75;
            Q75=sQuery(id+"F0.wireOp",EDGE,"E194");
            var Q76;
            Q76=sQuery(id+"F0.wireOp",EDGE,"E178");
            var Q77;
            Q77=sQuery(id+"F0.wireOp",EDGE,"E19");
            var Q78;
            Q78=sQuery(id+"F0.wireOp",EDGE,"E35");
            var Q79;
            Q79=sQuery(id+"F0.wireOp",EDGE,"E195");
            var Q80;
            Q80=sQuery(id+"F0.wireOp",EDGE,"E179");
            var Q81;
            Q81=sQuery(id+"F0.wireOp",EDGE,"E163");
            var Q82;
            Q82=sQuery(id+"F0.wireOp",EDGE,"E259");
            var Q83;
            Q83=sQuery(id+"F0.wireOp",EDGE,"E182");
            var Q84;
            Q84=sQuery(id+"F0.wireOp",EDGE,"E217");
            var Q85;
            Q85=sQuery(id+"F0.wireOp",EDGE,"E124");
            var Q86;
            Q86=sQuery(id+"F0.wireOp",EDGE,"E96");
            var Q87;
            Q87=sQuery(id+"F0.wireOp",EDGE,"E148");
            var Q88;
            Q88=sQuery(id+"F0.wireOp",EDGE,"E212");
            var Q89;
            Q89=sQuery(id+"F0.wireOp",EDGE,"E180");
            var Q90;
            Q90=sQuery(id+"F0.wireOp",EDGE,"E260");
            var Q91;
            Q91=sQuery(id+"F0.wireOp",EDGE,"E228");
            var Q92;
            Q92=sQuery(id+"F0.wireOp",EDGE,"E69");
            var Q93;
            Q93=sQuery(id+"F0.wireOp",EDGE,"E133");
            var Q94;
            Q94=sQuery(id+"F0.wireOp",EDGE,"E197");
            var Q95;
            Q95=sQuery(id+"F0.wireOp",EDGE,"E181");
            var Q96;
            Q96=sQuery(id+"F0.wireOp",EDGE,"E165");
            var Q97;
            Q97=sQuery(id+"F0.wireOp",EDGE,"E261");
            var Q98;
            Q98=sQuery(id+"F0.wireOp",EDGE,"E48");
            var Q99;
            Q99=sQuery(id+"F0.wireOp",EDGE,"E38");
            var Q100;
            Q100=sQuery(id+"F0.wireOp",EDGE,"E150");
            var Q101;
            Q101=sQuery(id+"F0.wireOp",EDGE,"E102");
            var Q102;
            Q102=sQuery(id+"F0.wireOp",EDGE,"E198");
            var Q103;
            Q103=sQuery(id+"F0.wireOp",EDGE,"E166");
            var Q104;
            Q104=sQuery(id+"F0.wireOp",EDGE,"E262");
            var Q105;
            Q105=sQuery(id+"F0.wireOp",EDGE,"E39");
            var Q106;
            Q106=sQuery(id+"F0.wireOp",EDGE,"E103");
            var Q107;
            Q107=sQuery(id+"F0.wireOp",EDGE,"E167");
            var Q108;
            Q108=sQuery(id+"F0.wireOp",EDGE,"E151");
            var Q109;
            Q109=sQuery(id+"F0.wireOp",EDGE,"E231");
            var Q110;
            Q110=sQuery(id+"F0.wireOp",EDGE,"E199");
            var Q111;
            Q111=sQuery(id+"F0.wireOp",EDGE,"E40");
            var Q112;
            Q112=sQuery(id+"F0.wireOp",EDGE,"E104");
            var Q113;
            Q113=sQuery(id+"F0.wireOp",EDGE,"E168");
            var Q114;
            Q114=sQuery(id+"F0.wireOp",EDGE,"E248");
            var Q115;
            Q115=sQuery(id+"F0.wireOp",EDGE,"E232");
            var Q116;
            Q116=sQuery(id+"F0.wireOp",EDGE,"E200");
            var Q117;
            Q117=sQuery(id+"F0.wireOp",EDGE,"E57");
            var Q118;
            Q118=sQuery(id+"F0.wireOp",EDGE,"E105");
            var Q119;
            Q119=sQuery(id+"F0.wireOp",EDGE,"E169");
            var Q120;
            Q120=sQuery(id+"F0.wireOp",EDGE,"E249");
            var Q121;
            Q121=sQuery(id+"F0.wireOp",EDGE,"E58");
            var Q122;
            Q122=sQuery(id+"F0.wireOp",EDGE,"E42");
            var Q123;
            Q123=sQuery(id+"F0.wireOp",EDGE,"E26");
            var Q124;
            Q124=sQuery(id+"F0.wireOp",EDGE,"E106");
            var Q125;
            Q125=sQuery(id+"F0.wireOp",EDGE,"E170");
            var Q126;
            Q126=sQuery(id+"F0.wireOp",EDGE,"E250");
            var Q127;
            Q127=sQuery(id+"F0.wireOp",EDGE,"E218");
            var Q128;
            Q128=sQuery(id+"F0.wireOp",EDGE,"E43");
            var Q129;
            Q129=sQuery(id+"F0.wireOp",EDGE,"E107");
            var Q130;
            Q130=sQuery(id+"F0.wireOp",EDGE,"E84");
            var Q131;
            Q131=sQuery(id+"F0.wireOp",EDGE,"E91");
            var Q132;
            Q132=sQuery(id+"F0.wireOp",EDGE,"E68");
            var Q133;
            Q133=sQuery(id+"F0.wireOp",EDGE,"E171");
            var Q134;
            Q134=sQuery(id+"F0.wireOp",EDGE,"E139");
            var Q135;
            Q135=sQuery(id+"F0.wireOp",EDGE,"E251");
            var Q136;
            Q136=sQuery(id+"F0.wireOp",EDGE,"E219");
            var Q137;
            Q137=sQuery(id+"F0.wireOp",EDGE,"E235");
            var Q138;
            Q138=sQuery(id+"F0.wireOp",EDGE,"E60");
            var Q139;
            Q139=sQuery(id+"F0.wireOp",EDGE,"E44");
            var Q140;
            Q140=sQuery(id+"F0.wireOp",EDGE,"E28");
            var Q141;
            Q141=sQuery(id+"F0.wireOp",EDGE,"E108");
            var Q142;
            Q142=sQuery(id+"F0.wireOp",EDGE,"E92");
            var Q143;
            Q143=sQuery(id+"F0.wireOp",EDGE,"E140");
            var Q144;
            Q144=sQuery(id+"F0.wireOp",EDGE,"E252");
            var Q145;
            Q145=sQuery(id+"F0.wireOp",EDGE,"E236");
            var Q146;
            Q146=sQuery(id+"F0.wireOp",EDGE,"E220");
            var Q147;
            Q147=sQuery(id+"F0.wireOp",EDGE,"E204");
            var Q148;
            Q148=sQuery(id+"F0.wireOp",EDGE,"E13");
            var Q149;
            Q149=sQuery(id+"F0.wireOp",EDGE,"E2");
            var Q150;
            Q150=sQuery(id+"F0.wireOp",EDGE,"E3");
            var Q151;
            Q151=sQuery(id+"F0.wireOp",EDGE,"E4");
            var Q152;
            Q152=sQuery(id+"F0.wireOp",EDGE,"E5");
            var Q153;
            Q153=sQuery(id+"F0.wireOp",EDGE,"E8");
            var Q154;
            Q154=sQuery(id+"F0.wireOp",EDGE,"E9");
            var Q155;
            Q155=sQuery(id+"F0.wireOp",EDGE,"E10");
            var Q156;
            Q156=sQuery(id+"F0.wireOp",EDGE,"E11");
            var Q157;
            Q157=sQuery(id+"F0.wireOp",EDGE,"E12");
            var Q158;
            Q158=sQuery(id+"F0.wireOp",EDGE,"E61");
            var Q159;
            Q159=sQuery(id+"F0.wireOp",EDGE,"E29");
            var Q160;
            Q160=sQuery(id+"F0.wireOp",EDGE,"E93");
            var Q161;
            Q161=sQuery(id+"F0.wireOp",EDGE,"E173");
            var Q162;
            Q162=sQuery(id+"F0.wireOp",EDGE,"E253");
            var Q163;
            Q163=sQuery(id+"F0.wireOp",EDGE,"E237");
            var Q164;
            Q164=sQuery(id+"F0.wireOp",EDGE,"E221");
            var Q165;
            Q165=sQuery(id+"F0.wireOp",EDGE,"E30");
            var Q166;
            Q166=sQuery(id+"F0.wireOp",EDGE,"E94");
            var Q167;
            Q167=sQuery(id+"F0.wireOp",EDGE,"E206");
            var Q168;
            Q168=sQuery(id+"F0.wireOp",EDGE,"E174");
            var Q169;
            Q169=sQuery(id+"F0.wireOp",EDGE,"E254");
            var Q170;
            Q170=sQuery(id+"F0.wireOp",EDGE,"E238");
            var Q171;
            Q171=sQuery(id+"F0.wireOp",EDGE,"E47");
            var Q172;
            Q172=sQuery(id+"F0.wireOp",EDGE,"E31");
            var Q173;
            Q173=sQuery(id+"F0.wireOp",EDGE,"E95");
            var Q174;
            Q174=sQuery(id+"F0.wireOp",EDGE,"E159");
            var Q175;
            Q175=sQuery(id+"F0.wireOp",EDGE,"E255");
            var Q176;
            Q176=sQuery(id+"F0.wireOp",EDGE,"E239");
            var Q177;
            Q177=sQuery(id+"F0.wireOp",EDGE,"E223");
            var Q178;
            Q178=sQuery(id+"F0.wireOp",EDGE,"E208");
            var Q179;
            Q179=sQuery(id+"F0.wireOp",EDGE,"E176");
            var Q180;
            Q180=sQuery(id+"F0.wireOp",EDGE,"E160");
            var Q181;
            Q181=sQuery(id+"F0.wireOp",EDGE,"E256");
            var Q182;
            Q182=sQuery(id+"F0.wireOp",EDGE,"E240");
            var Q183;
            Q183=sQuery(id+"F0.wireOp",EDGE,"E224");
            var Q184;
            Q184=sQuery(id+"F0.wireOp",EDGE,"E64");
            var Q185;
            Q185=sQuery(id+"F0.wireOp",EDGE,"E32");
            var Q186;
            Q186=sQuery(id+"F0.wireOp",EDGE,"E209");
            var Q187;
            Q187=sQuery(id+"F0.wireOp",EDGE,"E161");
            var Q188;
            Q188=sQuery(id+"F0.wireOp",EDGE,"E257");
            var Q189;
            Q189=sQuery(id+"F0.wireOp",EDGE,"E241");
            var Q190;
            Q190=sQuery(id+"F0.wireOp",EDGE,"E225");
            var Q191;
            Q191=sQuery(id+"F0.wireOp",EDGE,"E65");
            var Q192;
            Q192=sQuery(id+"F0.wireOp",EDGE,"E49");
            var Q193;
            Q193=sQuery(id+"F0.wireOp",EDGE,"E145");
            var Q194;
            Q194=sQuery(id+"F0.wireOp",EDGE,"E129");
            var Q195;
            Q195=sQuery(id+"F0.wireOp",EDGE,"E66");
            var Q196;
            Q196=sQuery(id+"F0.wireOp",EDGE,"E34");
            var Q197;
            Q197=sQuery(id+"F0.wireOp",EDGE,"E146");
            var Q198;
            Q198=sQuery(id+"F0.wireOp",EDGE,"E130");
            var Q199;
            Q199=sQuery(id+"F0.wireOp",EDGE,"E210");
            var Q200;
            Q200=sQuery(id+"F0.wireOp",EDGE,"E162");
            var Q201;
            Q201=sQuery(id+"F0.wireOp",EDGE,"E67");
            var Q202;
            Q202=sQuery(id+"F0.wireOp",EDGE,"E147");
            var Q203;
            Q203=sQuery(id+"F0.wireOp",EDGE,"E131");
            var Q204;
            Q204=sQuery(id+"F0.wireOp",EDGE,"E211");
            var Q205;
            Q205=sQuery(id+"F0.wireOp",EDGE,"E227");
            var Q206;
            Q206=sQuery(id+"F0.wireOp",EDGE,"E132");
            var Q207;
            Q207=sQuery(id+"F0.wireOp",EDGE,"E196");
            var Q208;
            Q208=sQuery(id+"F0.wireOp",EDGE,"E55");
            var Q209;
            Q209=sQuery(id+"F0.wireOp",EDGE,"E56");
            var Q210;
            Q210=sQuery(id+"F0.wireOp",EDGE,"E233");
            var Q211;
            Q211=sQuery(id+"F0.wireOp",EDGE,"E122");
            var Q212;
            Q212=sQuery(id+"F0.wireOp",EDGE,"E234");
            var Q213;
            Q213=sQuery(id+"F0.wireOp",EDGE,"E123");
            var Q214;
            Q214=sQuery(id+"F0.wireOp",EDGE,"E125");
            var Q215;
            Q215=sQuery(id+"F0.wireOp",EDGE,"E205");
            var Q216;
            Q216=sQuery(id+"F0.wireOp",EDGE,"E78");
            var Q217;
            Q217=sQuery(id+"F0.wireOp",EDGE,"E126");
            var Q218;
            Q218=sQuery(id+"F0.wireOp",EDGE,"E79");
            var Q219;
            Q219=sQuery(id+"F0.wireOp",EDGE,"E127");
            var Q220;
            Q220=sQuery(id+"F0.wireOp",EDGE,"E175");
            var Q221;
            Q221=sQuery(id+"F0.wireOp",EDGE,"E128");
            var Q222;
            Q222=sQuery(id+"F0.wireOp",EDGE,"E82");
            var Q223;
            Q223=sQuery(id+"F0.wireOp",EDGE,"E83");
            var Q224;
            Q224=sQuery(id+"F0.wireOp",EDGE,"E100");
            var Q225;
            Q225=sQuery(id+"F0.wireOp",EDGE,"E85");
            var Q226;
            Q226=sQuery(id+"F0.wireOp",EDGE,"E213");
            var Q227;
            Q227=sQuery(id+"F0.wireOp",EDGE,"E245");
            var Q228;
            Q228=sQuery(id+"F0.wireOp",EDGE,"E22");
            var Q229;
            Q229=sQuery(id+"F0.wireOp",EDGE,"E86");
            var Q230;
            Q230=sQuery(id+"F0.wireOp",EDGE,"E70");
            var Q231;
            Q231=sQuery(id+"F0.wireOp",EDGE,"E214");
            var Q232;
            Q232=sQuery(id+"F0.wireOp",EDGE,"E246");
            var Q233;
            Q233=sQuery(id+"F0.wireOp",EDGE,"E23");
            var Q234;
            Q234=sQuery(id+"F0.wireOp",EDGE,"E87");
            var Q235;
            Q235=sQuery(id+"F0.wireOp",EDGE,"E71");
            var Q236;
            Q236=sQuery(id+"F0.wireOp",EDGE,"E247");
            var Q237;
            Q237=sQuery(id+"F0.wireOp",EDGE,"E215");
            var Q238;
            Q238=sQuery(id+"F0.wireOp",EDGE,"E88");
            var Q239;
            Q239=sQuery(id+"F0.wireOp",EDGE,"E72");
            var Q240;
            Q240=sQuery(id+"F0.wireOp",EDGE,"E184");
            var Q241;
            Q241=sQuery(id+"F0.wireOp",EDGE,"E216");
            var Q242;
            Q242=sQuery(id+"F0.wireOp",EDGE,"E25");
            var Q243;
            Q243=sQuery(id+"F0.wireOp",EDGE,"E121");
            var Q244;
            Q244=sQuery(id+"F0.wireOp",EDGE,"E89");
            var Q245;
            Q245=sQuery(id+"F0.wireOp",EDGE,"E73");
            var Q246;
            Q246=sQuery(id+"F0.wireOp",EDGE,"E185");
            var Q247;
            Q247=sQuery(id+"F0.wireOp",EDGE,"E90");
            var Q248;
            Q248=sQuery(id+"F0.wireOp",EDGE,"E74");
            var Q249;
            Q249=sQuery(id+"F0.wireOp",EDGE,"E75");
            var Q250;
            Q250=sQuery(id+"F0.wireOp",EDGE,"E76");
            var Q251;
            Q251=sQuery(id+"F0.wireOp",EDGE,"E188");
            var Q252;
            Q252=sQuery(id+"F0.wireOp",EDGE,"E77");
            var Q253;
            Q253=sQuery(id+"F0.wireOp",EDGE,"E141");
            var Q254;
            Q254=sQuery(id+"F0.wireOp",EDGE,"E189");
            var Q255;
            Q255=sQuery(id+"F0.wireOp",EDGE,"E142");
            var Q256;
            Q256=sQuery(id+"F0.wireOp",EDGE,"E158");
            var Q257;
            Q257=sQuery(id+"F0.wireOp",EDGE,"E63");
            var Q258;
            Q258=sQuery(id+"F0.wireOp",EDGE,"E143");
            var Q259;
            Q259=sQuery(id+"F0.wireOp",EDGE,"E144");
            var Q260;
            Q260=sQuery(id+"F0.wireOp",EDGE,"E80");
            var Q261;
            Q261=sQuery(id+"F0.wireOp",EDGE,"E81");
            var Q262;
            Q262=sQuery(id+"F0.wireOp",EDGE,"E97");
            var Q263;
            Q263=sQuery(id+"F0.wireOp",EDGE,"E242");
            var Q264;
            Q264=sQuery(id+"F0.wireOp",EDGE,"E114");
            var Q265;
            Q265=sQuery(id+"F0.wireOp",EDGE,"E98");
            var Q266;
            Q266=sQuery(id+"F0.wireOp",EDGE,"E51");
            var Q267;
            Q267=sQuery(id+"F0.wireOp",EDGE,"E115");
            var Q268;
            Q268=sQuery(id+"F0.wireOp",EDGE,"E99");
            var Q269;
            Q269=sQuery(id+"F0.wireOp",EDGE,"E244");
            var Q270;
            Q270=sQuery(id+"F0.wireOp",EDGE,"E62");
            var Q271;
            Q271=sQuery(id+"F0.wireOp",EDGE,"E112");
            var Q272;
            Q272=sQuery(id+"F0.wireOp",EDGE,"E113");
            var Q273;
            Q273=sQuery(id+"F0.wireOp",EDGE,"E50");
            var Q274;
            Q274=sQuery(id+"F0.wireOp",EDGE,"E243");
            extrude(context, id + "F1", {"entities" : qUnion([Q0, Q1, Q2, Q3, Q4, Q5, Q6, Q7, Q8, Q9, Q10, Q11, Q12, Q13, Q14, Q15, Q16, Q17, Q18]), "surfaceEntities" : qUnion([Q19, Q20, Q21, Q22, Q23, Q24, Q25, Q26, Q27, Q28, Q29, Q30, Q31, Q32, Q33, Q34, Q35, Q36, Q37, Q38, Q39, Q40, Q41, Q42, Q43, Q44, Q45, Q46, Q47, Q48, Q49, Q50, Q51, Q52, Q53, Q54, Q55, Q56, Q57, Q58, Q59, Q60, Q61, Q62, Q63, Q64, Q65, Q66, Q67, Q68, Q69, Q70, Q71, Q72, Q73, Q74, Q75, Q76, Q77, Q78, Q79, Q80, Q81, Q82, Q83, Q84, Q85, Q86, Q87, Q88, Q89, Q90, Q91, Q92, Q93, Q94, Q95, Q96, Q97, Q98, Q99, Q100, Q101, Q102, Q103, Q104, Q105, Q106, Q107, Q108, Q109, Q110, Q111, Q112, Q113, Q114, Q115, Q116, Q117, Q118, Q119, Q120, Q121, Q122, Q123, Q124, Q125, Q126, Q127, Q128, Q129, Q130, Q131, Q132, Q133, Q134, Q135, Q136, Q137, Q138, Q139, Q140, Q141, Q142, Q143, Q144, Q145, Q146, Q147, Q148, Q149, Q150, Q151, Q152, Q153, Q154, Q155, Q156, Q157, Q158, Q159, Q160, Q161, Q162, Q163, Q164, Q165, Q166, Q167, Q168, Q169, Q170, Q171, Q172, Q173, Q174, Q175, Q176, Q177, Q178, Q179, Q180, Q181, Q182, Q183, Q184, Q185, Q186, Q187, Q188, Q189, Q190, Q191, Q192, Q193, Q194, Q195, Q196, Q197, Q198, Q199, Q200, Q201, Q202, Q203, Q204, Q205, Q206, Q207, Q208, Q209, Q210, Q211, Q212, Q213, Q214, Q215, Q216, Q217, Q218, Q219, Q220, Q221, Q222, Q223, Q224, Q225, Q226, Q227, Q228, Q229, Q230, Q231, Q232, Q233, Q234, Q235, Q236, Q237, Q238, Q239, Q240, Q241, Q242, Q243, Q244, Q245, Q246, Q247, Q248, Q249, Q250, Q251, Q252, Q253, Q254, Q255, Q256, Q257, Q258, Q259, Q260, Q261, Q262, Q263, Q264, Q265, Q266, Q267, Q268, Q269, Q270, Q271, Q272, Q273, Q274]), "depth" : 3 * mm});
        }
        {
            var Q0;
            Q0=makeQuery(id+"F1.opExtrude","CAP_FACE",FACE,{"disambiguationData":[OSD([sQuery(id+"F0.wireOp",EDGE,"E0"),sQuery(id+"F0.wireOp",EDGE,"E1"),sQuery(id+"F0.wireOp",EDGE,"E2"),sQuery(id+"F0.wireOp",EDGE,"E3"),sQuery(id+"F0.wireOp",EDGE,"E4"),sQuery(id+"F0.wireOp",EDGE,"E5"),sQuery(id+"F0.wireOp",EDGE,"E6"),sQuery(id+"F0.wireOp",EDGE,"E7"),sQuery(id+"F0.wireOp",EDGE,"E8"),sQuery(id+"F0.wireOp",EDGE,"E9"),sQuery(id+"F0.wireOp",EDGE,"E10"),sQuery(id+"F0.wireOp",EDGE,"E11"),sQuery(id+"F0.wireOp",EDGE,"E12"),sQuery(id+"F0.wireOp",EDGE,"E13"),sQuery(id+"F0.wireOp",EDGE,"E14"),sQuery(id+"F0.wireOp",EDGE,"E15"),sQuery(id+"F0.wireOp",EDGE,"E16"),sQuery(id+"F0.wireOp",EDGE,"E17"),sQuery(id+"F0.wireOp",EDGE,"E18"),sQuery(id+"F0.wireOp",EDGE,"E19"),sQuery(id+"F0.wireOp",EDGE,"E20"),sQuery(id+"F0.wireOp",EDGE,"E21"),sQuery(id+"F0.wireOp",EDGE,"E22"),sQuery(id+"F0.wireOp",EDGE,"E34"),sQuery(id+"F0.wireOp",EDGE,"E35"),sQuery(id+"F0.wireOp",EDGE,"E36"),sQuery(id+"F0.wireOp",EDGE,"E37"),sQuery(id+"F0.wireOp",EDGE,"E38"),sQuery(id+"F0.wireOp",EDGE,"E39"),sQuery(id+"F0.wireOp",EDGE,"E40"),sQuery(id+"F0.wireOp",EDGE,"E41"),sQuery(id+"F0.wireOp",EDGE,"E50"),sQuery(id+"F0.wireOp",EDGE,"E51"),sQuery(id+"F0.wireOp",EDGE,"E52"),sQuery(id+"F0.wireOp",EDGE,"E53"),sQuery(id+"F0.wireOp",EDGE,"E54"),sQuery(id+"F0.wireOp",EDGE,"E55"),sQuery(id+"F0.wireOp",EDGE,"E63"),sQuery(id+"F0.wireOp",EDGE,"E64"),sQuery(id+"F0.wireOp",EDGE,"E65"),sQuery(id+"F0.wireOp",EDGE,"E66"),sQuery(id+"F0.wireOp",EDGE,"E67"),sQuery(id+"F0.wireOp",EDGE,"E68"),sQuery(id+"F0.wireOp",EDGE,"E69"),sQuery(id+"F0.wireOp",EDGE,"E70"),sQuery(id+"F0.wireOp",EDGE,"E71"),sQuery(id+"F0.wireOp",EDGE,"E72"),sQuery(id+"F0.wireOp",EDGE,"E87"),sQuery(id+"F0.wireOp",EDGE,"E88"),sQuery(id+"F0.wireOp",EDGE,"E89"),sQuery(id+"F0.wireOp",EDGE,"E90"),sQuery(id+"F0.wireOp",EDGE,"E91"),sQuery(id+"F0.wireOp",EDGE,"E92"),sQuery(id+"F0.wireOp",EDGE,"E93"),sQuery(id+"F0.wireOp",EDGE,"E94"),sQuery(id+"F0.wireOp",EDGE,"E95"),sQuery(id+"F0.wireOp",EDGE,"E105"),sQuery(id+"F0.wireOp",EDGE,"E106"),sQuery(id+"F0.wireOp",EDGE,"E117"),sQuery(id+"F0.wireOp",EDGE,"E118"),sQuery(id+"F0.wireOp",EDGE,"E119"),sQuery(id+"F0.wireOp",EDGE,"E120"),sQuery(id+"F0.wireOp",EDGE,"E121"),sQuery(id+"F0.wireOp",EDGE,"E132"),sQuery(id+"F0.wireOp",EDGE,"E133"),sQuery(id+"F0.wireOp",EDGE,"E134"),sQuery(id+"F0.wireOp",EDGE,"E135"),sQuery(id+"F0.wireOp",EDGE,"E136"),sQuery(id+"F0.wireOp",EDGE,"E137"),sQuery(id+"F0.wireOp",EDGE,"E138"),sQuery(id+"F0.wireOp",EDGE,"E139"),sQuery(id+"F0.wireOp",EDGE,"E140"),sQuery(id+"F0.wireOp",EDGE,"E141"),sQuery(id+"F0.wireOp",EDGE,"E157"),sQuery(id+"F0.wireOp",EDGE,"E158"),sQuery(id+"F0.wireOp",EDGE,"E159"),sQuery(id+"F0.wireOp",EDGE,"E160"),sQuery(id+"F0.wireOp",EDGE,"E161"),sQuery(id+"F0.wireOp",EDGE,"E162"),sQuery(id+"F0.wireOp",EDGE,"E163"),sQuery(id+"F0.wireOp",EDGE,"E164"),sQuery(id+"F0.wireOp",EDGE,"E169"),sQuery(id+"F0.wireOp",EDGE,"E170"),sQuery(id+"F0.wireOp",EDGE,"E171"),sQuery(id+"F0.wireOp",EDGE,"E172"),sQuery(id+"F0.wireOp",EDGE,"E173"),sQuery(id+"F0.wireOp",EDGE,"E174"),sQuery(id+"F0.wireOp",EDGE,"E175"),sQuery(id+"F0.wireOp",EDGE,"E180"),sQuery(id+"F0.wireOp",EDGE,"E181"),sQuery(id+"F0.wireOp",EDGE,"E182"),sQuery(id+"F0.wireOp",EDGE,"E183"),sQuery(id+"F0.wireOp",EDGE,"E184"),sQuery(id+"F0.wireOp",EDGE,"E185"),sQuery(id+"F0.wireOp",EDGE,"E186"),sQuery(id+"F0.wireOp",EDGE,"E187"),sQuery(id+"F0.wireOp",EDGE,"E188"),sQuery(id+"F0.wireOp",EDGE,"E189"),sQuery(id+"F0.wireOp",EDGE,"E190"),sQuery(id+"F0.wireOp",EDGE,"E191"),sQuery(id+"F0.wireOp",EDGE,"E192"),sQuery(id+"F0.wireOp",EDGE,"E193"),sQuery(id+"F0.wireOp",EDGE,"E194"),sQuery(id+"F0.wireOp",EDGE,"E195"),sQuery(id+"F0.wireOp",EDGE,"E196"),sQuery(id+"F0.wireOp",EDGE,"E209"),sQuery(id+"F0.wireOp",EDGE,"E210"),sQuery(id+"F0.wireOp",EDGE,"E211"),sQuery(id+"F0.wireOp",EDGE,"E212"),sQuery(id+"F0.wireOp",EDGE,"E213"),sQuery(id+"F0.wireOp",EDGE,"E219"),sQuery(id+"F0.wireOp",EDGE,"E220"),sQuery(id+"F0.wireOp",EDGE,"E221"),sQuery(id+"F0.wireOp",EDGE,"E222"),sQuery(id+"F0.wireOp",EDGE,"E223"),sQuery(id+"F0.wireOp",EDGE,"E224"),sQuery(id+"F0.wireOp",EDGE,"E225"),sQuery(id+"F0.wireOp",EDGE,"E226"),sQuery(id+"F0.wireOp",EDGE,"E227"),sQuery(id+"F0.wireOp",EDGE,"E228"),sQuery(id+"F0.wireOp",EDGE,"E229"),sQuery(id+"F0.wireOp",EDGE,"E230"),sQuery(id+"F0.wireOp",EDGE,"E231"),sQuery(id+"F0.wireOp",EDGE,"E232"),sQuery(id+"F0.wireOp",EDGE,"E233"),sQuery(id+"F0.wireOp",EDGE,"E234"),sQuery(id+"F0.wireOp",EDGE,"E243"),sQuery(id+"F0.wireOp",EDGE,"E244"),sQuery(id+"F0.wireOp",EDGE,"E245"),sQuery(id+"F0.wireOp",EDGE,"E246"),sQuery(id+"F0.wireOp",EDGE,"E247"),sQuery(id+"F0.wireOp",EDGE,"E248"),sQuery(id+"F0.wireOp",EDGE,"E249"),sQuery(id+"F0.wireOp",EDGE,"E250"),sQuery(id+"F0.wireOp",EDGE,"E251"),sQuery(id+"F0.wireOp",EDGE,"E252"),sQuery(id+"F0.wireOp",EDGE,"E253"),sQuery(id+"F0.wireOp",EDGE,"E254"),sQuery(id+"F0.wireOp",EDGE,"E255"),sQuery(id+"F0.wireOp",EDGE,"E256"),sQuery(id+"F0.wireOp",EDGE,"E257"),sQuery(id+"F0.wireOp",EDGE,"E258"),sQuery(id+"F0.wireOp",EDGE,"E259"),sQuery(id+"F0.wireOp",EDGE,"E260"),sQuery(id+"F0.wireOp",EDGE,"E261"),sQuery(id+"F0.wireOp",EDGE,"E262")])],"isStart":false});
            var sketch = newSketch(context, id + "F2", { "sketchPlane" : qUnion([Q0])});
            skLineSegment(sketch, "E263", {"start": v(-26.63, -2.91) * mm, "end": v(-26.74, -2.83) * mm});
            skLineSegment(sketch, "E264", {"start": v(-26.74, -2.83) * mm, "end": v(-31.9, -2.83) * mm});
            skLineSegment(sketch, "E265", {"start": v(-31.9, -2.83) * mm, "end": v(-29.4, -0.5) * mm});
            skLineSegment(sketch, "E266", {"start": v(-29.4, -0.5) * mm, "end": v(-27.97, 0.92) * mm});
            skLineSegment(sketch, "E267", {"start": v(-27.97, 0.92) * mm, "end": v(-26.93, 2.3) * mm});
            skLineSegment(sketch, "E268", {"start": v(-26.93, 2.3) * mm, "end": v(-26.3, 3.74) * mm});
            skLineSegment(sketch, "E269", {"start": v(-26.3, 3.74) * mm, "end": v(-26.08, 5.37) * mm});
            skLineSegment(sketch, "E270", {"start": v(-26.08, 5.37) * mm, "end": v(-26.18, 6.48) * mm});
            skLineSegment(sketch, "E271", {"start": v(-26.18, 6.48) * mm, "end": v(-26.48, 7.46) * mm});
            skLineSegment(sketch, "E272", {"start": v(-26.48, 7.46) * mm, "end": v(-26.97, 8.31) * mm});
            skLineSegment(sketch, "E273", {"start": v(-26.97, 8.31) * mm, "end": v(-27.63, 9.02) * mm});
            skLineSegment(sketch, "E274", {"start": v(-27.63, 9.02) * mm, "end": v(-28.47, 9.59) * mm});
            skLineSegment(sketch, "E275", {"start": v(-28.47, 9.59) * mm, "end": v(-29.47, 10) * mm});
            skLineSegment(sketch, "E276", {"start": v(-29.47, 10) * mm, "end": v(-30.63, 10.25) * mm});
            skLineSegment(sketch, "E277", {"start": v(-30.63, 10.25) * mm, "end": v(-31.93, 10.34) * mm});
            skLineSegment(sketch, "E278", {"start": v(-31.93, 10.34) * mm, "end": v(-35.01, 9.95) * mm});
            skLineSegment(sketch, "E279", {"start": v(-35.01, 9.95) * mm, "end": v(-37.78, 8.76) * mm});
            skLineSegment(sketch, "E280", {"start": v(-37.78, 8.76) * mm, "end": v(-37.84, 8.63) * mm});
            skLineSegment(sketch, "E281", {"start": v(-37.84, 8.63) * mm, "end": v(-37.26, 4.54) * mm});
            skLineSegment(sketch, "E282", {"start": v(-37.26, 4.54) * mm, "end": v(-37.18, 4.43) * mm});
            skLineSegment(sketch, "E283", {"start": v(-37.18, 4.43) * mm, "end": v(-37.07, 4.43) * mm});
            skLineSegment(sketch, "E284", {"start": v(-37.07, 4.43) * mm, "end": v(-34.78, 5.61) * mm});
            skLineSegment(sketch, "E285", {"start": v(-34.78, 5.61) * mm, "end": v(-32.76, 6) * mm});
            skLineSegment(sketch, "E286", {"start": v(-32.76, 6) * mm, "end": v(-32.06, 5.92) * mm});
            skLineSegment(sketch, "E287", {"start": v(-32.06, 5.92) * mm, "end": v(-31.54, 5.67) * mm});
            skLineSegment(sketch, "E288", {"start": v(-31.54, 5.67) * mm, "end": v(-31.22, 5.28) * mm});
            skLineSegment(sketch, "E289", {"start": v(-31.22, 5.28) * mm, "end": v(-31.1, 4.76) * mm});
            skLineSegment(sketch, "E290", {"start": v(-31.1, 4.76) * mm, "end": v(-31.46, 3.54) * mm});
            skLineSegment(sketch, "E291", {"start": v(-31.46, 3.54) * mm, "end": v(-32.54, 2.25) * mm});
            skLineSegment(sketch, "E292", {"start": v(-32.54, 2.25) * mm, "end": v(-38.14, -3.24) * mm});
            skLineSegment(sketch, "E293", {"start": v(-38.14, -3.24) * mm, "end": v(-38.17, -3.33) * mm});
            skLineSegment(sketch, "E294", {"start": v(-38.17, -3.33) * mm, "end": v(-38.17, -6.8) * mm});
            skLineSegment(sketch, "E295", {"start": v(-38.17, -6.8) * mm, "end": v(-38.03, -6.94) * mm});
            skLineSegment(sketch, "E296", {"start": v(-38.03, -6.94) * mm, "end": v(-25.25, -6.94) * mm});
            skLineSegment(sketch, "E297", {"start": v(-25.25, -6.94) * mm, "end": v(-25.14, -6.89) * mm});
            skLineSegment(sketch, "E298", {"start": v(-25.14, -6.89) * mm, "end": v(-25.14, -6.78) * mm});
            skLineSegment(sketch, "E299", {"start": v(-25.14, -6.78) * mm, "end": v(-26.63, -2.91) * mm});
            skLineSegment(sketch, "E300", {"start": v(-16.2, 5.84) * mm, "end": v(-17.26, 5.7) * mm});
            skLineSegment(sketch, "E301", {"start": v(-17.26, 5.7) * mm, "end": v(-18.19, 5.31) * mm});
            skLineSegment(sketch, "E302", {"start": v(-18.19, 5.31) * mm, "end": v(-19, 4.76) * mm});
            skLineSegment(sketch, "E303", {"start": v(-19, 4.76) * mm, "end": v(-19.73, 4.1) * mm});
            skLineSegment(sketch, "E304", {"start": v(-19.73, 4.1) * mm, "end": v(-19.95, 5.48) * mm});
            skLineSegment(sketch, "E305", {"start": v(-19.95, 5.48) * mm, "end": v(-20.1, 5.59) * mm});
            skLineSegment(sketch, "E306", {"start": v(-20.1, 5.59) * mm, "end": v(-24.04, 5.59) * mm});
            skLineSegment(sketch, "E307", {"start": v(-24.04, 5.59) * mm, "end": v(-24.18, 5.45) * mm});
            skLineSegment(sketch, "E308", {"start": v(-24.18, 5.45) * mm, "end": v(-24.18, -6.8) * mm});
            skLineSegment(sketch, "E309", {"start": v(-24.18, -6.8) * mm, "end": v(-24.04, -6.94) * mm});
            skLineSegment(sketch, "E310", {"start": v(-24.04, -6.94) * mm, "end": v(-19.62, -6.94) * mm});
            skLineSegment(sketch, "E311", {"start": v(-19.62, -6.94) * mm, "end": v(-19.49, -6.8) * mm});
            skLineSegment(sketch, "E312", {"start": v(-19.49, -6.8) * mm, "end": v(-19.49, 1.06) * mm});
            skLineSegment(sketch, "E313", {"start": v(-19.49, 1.06) * mm, "end": v(-18.8, 1.57) * mm});
            skLineSegment(sketch, "E314", {"start": v(-18.8, 1.57) * mm, "end": v(-18.16, 1.73) * mm});
            skLineSegment(sketch, "E315", {"start": v(-18.16, 1.73) * mm, "end": v(-17.7, 1.62) * mm});
            skLineSegment(sketch, "E316", {"start": v(-17.7, 1.62) * mm, "end": v(-17.44, 1.36) * mm});
            skLineSegment(sketch, "E317", {"start": v(-17.44, 1.36) * mm, "end": v(-17.31, 1) * mm});
            skLineSegment(sketch, "E318", {"start": v(-17.31, 1) * mm, "end": v(-17.28, 0.62) * mm});
            skLineSegment(sketch, "E319", {"start": v(-17.28, 0.62) * mm, "end": v(-17.28, -6.78) * mm});
            skLineSegment(sketch, "E320", {"start": v(-17.28, -6.78) * mm, "end": v(-17.14, -6.91) * mm});
            skLineSegment(sketch, "E321", {"start": v(-17.14, -6.91) * mm, "end": v(-12.72, -6.91) * mm});
            skLineSegment(sketch, "E322", {"start": v(-12.72, -6.91) * mm, "end": v(-12.59, -6.78) * mm});
            skLineSegment(sketch, "E323", {"start": v(-12.59, -6.78) * mm, "end": v(-12.59, 1.86) * mm});
            skLineSegment(sketch, "E324", {"start": v(-12.59, 1.86) * mm, "end": v(-12.84, 3.57) * mm});
            skLineSegment(sketch, "E325", {"start": v(-12.84, 3.57) * mm, "end": v(-13.53, 4.81) * mm});
            skLineSegment(sketch, "E326", {"start": v(-13.53, 4.81) * mm, "end": v(-14.66, 5.58) * mm});
            skLineSegment(sketch, "E327", {"start": v(-14.66, 5.58) * mm, "end": v(-16.2, 5.84) * mm});
            skLineSegment(sketch, "E328", {"start": v(-8.39, 11.44) * mm, "end": v(-9.43, 11.26) * mm});
            skLineSegment(sketch, "E329", {"start": v(-9.43, 11.26) * mm, "end": v(-10.24, 10.76) * mm});
            skLineSegment(sketch, "E330", {"start": v(-10.24, 10.76) * mm, "end": v(-10.77, 10) * mm});
            skLineSegment(sketch, "E331", {"start": v(-10.77, 10) * mm, "end": v(-10.96, 9.01) * mm});
            skLineSegment(sketch, "E332", {"start": v(-10.96, 9.01) * mm, "end": v(-10.77, 8.04) * mm});
            skLineSegment(sketch, "E333", {"start": v(-10.77, 8.04) * mm, "end": v(-10.24, 7.28) * mm});
            skLineSegment(sketch, "E334", {"start": v(-10.24, 7.28) * mm, "end": v(-9.43, 6.79) * mm});
            skLineSegment(sketch, "E335", {"start": v(-9.43, 6.79) * mm, "end": v(-8.39, 6.61) * mm});
            skLineSegment(sketch, "E336", {"start": v(-8.39, 6.61) * mm, "end": v(-7.35, 6.79) * mm});
            skLineSegment(sketch, "E337", {"start": v(-7.35, 6.79) * mm, "end": v(-6.54, 7.28) * mm});
            skLineSegment(sketch, "E338", {"start": v(-6.54, 7.28) * mm, "end": v(-6.01, 8.04) * mm});
            skLineSegment(sketch, "E339", {"start": v(-6.01, 8.04) * mm, "end": v(-5.82, 9.01) * mm});
            skLineSegment(sketch, "E340", {"start": v(-5.82, 9.01) * mm, "end": v(-6, 10) * mm});
            skLineSegment(sketch, "E341", {"start": v(-6, 10) * mm, "end": v(-6.53, 10.76) * mm});
            skLineSegment(sketch, "E342", {"start": v(-6.53, 10.76) * mm, "end": v(-7.34, 11.26) * mm});
            skLineSegment(sketch, "E343", {"start": v(-7.34, 11.26) * mm, "end": v(-8.39, 11.44) * mm});
            skLineSegment(sketch, "E344", {"start": v(-6.18, 5.59) * mm, "end": v(-10.6, 5.59) * mm});
            skLineSegment(sketch, "E345", {"start": v(-10.6, 5.59) * mm, "end": v(-10.74, 5.45) * mm});
            skLineSegment(sketch, "E346", {"start": v(-10.74, 5.45) * mm, "end": v(-10.74, -6.8) * mm});
            skLineSegment(sketch, "E347", {"start": v(-10.74, -6.8) * mm, "end": v(-10.6, -6.94) * mm});
            skLineSegment(sketch, "E348", {"start": v(-10.6, -6.94) * mm, "end": v(-6.18, -6.94) * mm});
            skLineSegment(sketch, "E349", {"start": v(-6.18, -6.94) * mm, "end": v(-6.04, -6.8) * mm});
            skLineSegment(sketch, "E350", {"start": v(-6.04, -6.8) * mm, "end": v(-6.04, 5.48) * mm});
            skLineSegment(sketch, "E351", {"start": v(-6.04, 5.48) * mm, "end": v(-6.18, 5.59) * mm});
            skLineSegment(sketch, "E352", {"start": v(8.47, 5.92) * mm, "end": v(8.36, 5.92) * mm});
            skLineSegment(sketch, "E353", {"start": v(8.36, 5.92) * mm, "end": v(5.13, 4.57) * mm});
            skLineSegment(sketch, "E354", {"start": v(5.13, 4.57) * mm, "end": v(3.31, 5.48) * mm});
            skLineSegment(sketch, "E355", {"start": v(3.31, 5.48) * mm, "end": v(1.08, 5.78) * mm});
            skLineSegment(sketch, "E356", {"start": v(1.08, 5.78) * mm, "end": v(-0.1, 5.7) * mm});
            skLineSegment(sketch, "E357", {"start": v(-0.1, 5.7) * mm, "end": v(-1.15, 5.46) * mm});
            skLineSegment(sketch, "E358", {"start": v(-1.15, 5.46) * mm, "end": v(-2.09, 5.06) * mm});
            skLineSegment(sketch, "E359", {"start": v(-2.09, 5.06) * mm, "end": v(-2.88, 4.53) * mm});
            skLineSegment(sketch, "E360", {"start": v(-2.88, 4.53) * mm, "end": v(-3.52, 3.88) * mm});
            skLineSegment(sketch, "E361", {"start": v(-3.52, 3.88) * mm, "end": v(-4, 3.1) * mm});
            skLineSegment(sketch, "E362", {"start": v(-4, 3.1) * mm, "end": v(-4.29, 2.23) * mm});
            skLineSegment(sketch, "E363", {"start": v(-4.29, 2.23) * mm, "end": v(-4.39, 1.26) * mm});
            skLineSegment(sketch, "E364", {"start": v(-4.39, 1.26) * mm, "end": v(-4.24, 0.16) * mm});
            skLineSegment(sketch, "E365", {"start": v(-4.24, 0.16) * mm, "end": v(-3.8, -0.8) * mm});
            skLineSegment(sketch, "E366", {"start": v(-3.8, -0.8) * mm, "end": v(-3.1, -1.61) * mm});
            skLineSegment(sketch, "E367", {"start": v(-3.1, -1.61) * mm, "end": v(-2.15, -2.25) * mm});
            skLineSegment(sketch, "E368", {"start": v(-2.15, -2.25) * mm, "end": v(-3.58, -3.41) * mm});
            skLineSegment(sketch, "E369", {"start": v(-3.58, -3.41) * mm, "end": v(-4.06, -4.68) * mm});
            skLineSegment(sketch, "E370", {"start": v(-4.06, -4.68) * mm, "end": v(-3.92, -5.38) * mm});
            skLineSegment(sketch, "E371", {"start": v(-3.92, -5.38) * mm, "end": v(-3.5, -6.03) * mm});
            skLineSegment(sketch, "E372", {"start": v(-3.5, -6.03) * mm, "end": v(-4.78, -7.15) * mm});
            skLineSegment(sketch, "E373", {"start": v(-4.78, -7.15) * mm, "end": v(-5.19, -8.49) * mm});
            skLineSegment(sketch, "E374", {"start": v(-5.19, -8.49) * mm, "end": v(-4.76, -9.7) * mm});
            skLineSegment(sketch, "E375", {"start": v(-4.76, -9.7) * mm, "end": v(-3.52, -10.63) * mm});
            skLineSegment(sketch, "E376", {"start": v(-3.52, -10.63) * mm, "end": v(-1.6, -11.23) * mm});
            skLineSegment(sketch, "E377", {"start": v(-1.6, -11.23) * mm, "end": v(0.94, -11.44) * mm});
            skLineSegment(sketch, "E378", {"start": v(0.94, -11.44) * mm, "end": v(3.92, -11.08) * mm});
            skLineSegment(sketch, "E379", {"start": v(3.92, -11.08) * mm, "end": v(6.25, -10.1) * mm});
            skLineSegment(sketch, "E380", {"start": v(6.25, -10.1) * mm, "end": v(7.76, -8.57) * mm});
            skLineSegment(sketch, "E381", {"start": v(7.76, -8.57) * mm, "end": v(8.3, -6.64) * mm});
            skLineSegment(sketch, "E382", {"start": v(8.3, -6.64) * mm, "end": v(8.07, -5.47) * mm});
            skLineSegment(sketch, "E383", {"start": v(8.07, -5.47) * mm, "end": v(7.35, -4.61) * mm});
            skLineSegment(sketch, "E384", {"start": v(7.35, -4.61) * mm, "end": v(6.12, -4.06) * mm});
            skLineSegment(sketch, "E385", {"start": v(6.12, -4.06) * mm, "end": v(4.36, -3.8) * mm});
            skLineSegment(sketch, "E386", {"start": v(4.36, -3.8) * mm, "end": v(1.55, -3.63) * mm});
            skLineSegment(sketch, "E387", {"start": v(1.55, -3.63) * mm, "end": v(0.69, -3.55) * mm});
            skLineSegment(sketch, "E388", {"start": v(0.69, -3.55) * mm, "end": v(0.2, -3.47) * mm});
            skLineSegment(sketch, "E389", {"start": v(0.2, -3.47) * mm, "end": v(0, -3.37) * mm});
            skLineSegment(sketch, "E390", {"start": v(0, -3.37) * mm, "end": v(-0.06, -3.24) * mm});
            skLineSegment(sketch, "E391", {"start": v(-0.06, -3.24) * mm, "end": v(0.08, -2.88) * mm});
            skLineSegment(sketch, "E392", {"start": v(0.08, -2.88) * mm, "end": v(1.24, -2.94) * mm});
            skLineSegment(sketch, "E393", {"start": v(1.24, -2.94) * mm, "end": v(2.38, -2.86) * mm});
            skLineSegment(sketch, "E394", {"start": v(2.38, -2.86) * mm, "end": v(3.42, -2.62) * mm});
            skLineSegment(sketch, "E395", {"start": v(3.42, -2.62) * mm, "end": v(4.34, -2.23) * mm});
            skLineSegment(sketch, "E396", {"start": v(4.34, -2.23) * mm, "end": v(5.12, -1.72) * mm});
            skLineSegment(sketch, "E397", {"start": v(5.12, -1.72) * mm, "end": v(5.76, -1.08) * mm});
            skLineSegment(sketch, "E398", {"start": v(5.76, -1.08) * mm, "end": v(6.23, -0.34) * mm});
            skLineSegment(sketch, "E399", {"start": v(6.23, -0.34) * mm, "end": v(6.52, 0.5) * mm});
            skLineSegment(sketch, "E400", {"start": v(6.52, 0.5) * mm, "end": v(6.62, 1.42) * mm});
            skLineSegment(sketch, "E401", {"start": v(6.62, 1.42) * mm, "end": v(6.54, 2.3) * mm});
            skLineSegment(sketch, "E402", {"start": v(6.54, 2.3) * mm, "end": v(8.47, 2.3) * mm});
            skLineSegment(sketch, "E403", {"start": v(8.47, 2.3) * mm, "end": v(8.55, 2.33) * mm});
            skLineSegment(sketch, "E404", {"start": v(8.55, 2.33) * mm, "end": v(8.58, 2.42) * mm});
            skLineSegment(sketch, "E405", {"start": v(8.58, 2.42) * mm, "end": v(8.55, 5.75) * mm});
            skLineSegment(sketch, "E406", {"start": v(8.55, 5.75) * mm, "end": v(8.47, 5.92) * mm});
            skLineSegment(sketch, "E407", {"start": v(2.46, 1.42) * mm, "end": v(2.36, 0.72) * mm});
            skLineSegment(sketch, "E408", {"start": v(2.36, 0.72) * mm, "end": v(2.1, 0.2) * mm});
            skLineSegment(sketch, "E409", {"start": v(2.1, 0.2) * mm, "end": v(1.68, -0.12) * mm});
            skLineSegment(sketch, "E410", {"start": v(1.68, -0.12) * mm, "end": v(1.1, -0.23) * mm});
            skLineSegment(sketch, "E411", {"start": v(1.1, -0.23) * mm, "end": v(0.55, -0.13) * mm});
            skLineSegment(sketch, "E412", {"start": v(0.55, -0.13) * mm, "end": v(0.14, 0.18) * mm});
            skLineSegment(sketch, "E413", {"start": v(0.14, 0.18) * mm, "end": v(-0.1, 0.69) * mm});
            skLineSegment(sketch, "E414", {"start": v(-0.1, 0.69) * mm, "end": v(-0.2, 1.37) * mm});
            skLineSegment(sketch, "E415", {"start": v(-0.2, 1.37) * mm, "end": v(-0.13, 1.98) * mm});
            skLineSegment(sketch, "E416", {"start": v(-0.13, 1.98) * mm, "end": v(0.1, 2.53) * mm});
            skLineSegment(sketch, "E417", {"start": v(0.1, 2.53) * mm, "end": v(0.5, 2.93) * mm});
            skLineSegment(sketch, "E418", {"start": v(0.5, 2.93) * mm, "end": v(1.1, 3.08) * mm});
            skLineSegment(sketch, "E419", {"start": v(1.1, 3.08) * mm, "end": v(1.66, 2.96) * mm});
            skLineSegment(sketch, "E420", {"start": v(1.66, 2.96) * mm, "end": v(2.09, 2.63) * mm});
            skLineSegment(sketch, "E421", {"start": v(2.09, 2.63) * mm, "end": v(2.36, 2.11) * mm});
            skLineSegment(sketch, "E422", {"start": v(2.36, 2.11) * mm, "end": v(2.46, 1.42) * mm});
            skLineSegment(sketch, "E423", {"start": v(1.3, -9.1) * mm, "end": v(0.06, -9.02) * mm});
            skLineSegment(sketch, "E424", {"start": v(0.06, -9.02) * mm, "end": v(-0.82, -8.79) * mm});
            skLineSegment(sketch, "E425", {"start": v(-0.82, -8.79) * mm, "end": v(-1.34, -8.4) * mm});
            skLineSegment(sketch, "E426", {"start": v(-1.34, -8.4) * mm, "end": v(-1.52, -7.88) * mm});
            skLineSegment(sketch, "E427", {"start": v(-1.52, -7.88) * mm, "end": v(-1.21, -7.05) * mm});
            skLineSegment(sketch, "E428", {"start": v(-1.21, -7.05) * mm, "end": v(-0.42, -7.14) * mm});
            skLineSegment(sketch, "E429", {"start": v(-0.42, -7.14) * mm, "end": v(0.6, -7.22) * mm});
            skLineSegment(sketch, "E430", {"start": v(0.6, -7.22) * mm, "end": v(2.6, -7.33) * mm});
            skLineSegment(sketch, "E431", {"start": v(2.6, -7.33) * mm, "end": v(3.33, -7.4) * mm});
            skLineSegment(sketch, "E432", {"start": v(3.33, -7.4) * mm, "end": v(3.77, -7.51) * mm});
            skLineSegment(sketch, "E433", {"start": v(3.77, -7.51) * mm, "end": v(3.98, -7.68) * mm});
            skLineSegment(sketch, "E434", {"start": v(3.98, -7.68) * mm, "end": v(4.03, -7.9) * mm});
            skLineSegment(sketch, "E435", {"start": v(4.03, -7.9) * mm, "end": v(3.83, -8.4) * mm});
            skLineSegment(sketch, "E436", {"start": v(3.83, -8.4) * mm, "end": v(3.26, -8.77) * mm});
            skLineSegment(sketch, "E437", {"start": v(3.26, -8.77) * mm, "end": v(2.4, -9) * mm});
            skLineSegment(sketch, "E438", {"start": v(2.4, -9) * mm, "end": v(1.3, -9.1) * mm});
            skLineSegment(sketch, "E439", {"start": v(17.44, 5.84) * mm, "end": v(16.5, 5.73) * mm});
            skLineSegment(sketch, "E440", {"start": v(16.5, 5.73) * mm, "end": v(15.65, 5.42) * mm});
            skLineSegment(sketch, "E441", {"start": v(15.65, 5.42) * mm, "end": v(14.88, 4.93) * mm});
            skLineSegment(sketch, "E442", {"start": v(14.88, 4.93) * mm, "end": v(14.13, 4.3) * mm});
            skLineSegment(sketch, "E443", {"start": v(14.13, 4.3) * mm, "end": v(14.13, 11.08) * mm});
            skLineSegment(sketch, "E444", {"start": v(14.13, 11.08) * mm, "end": v(14.07, 11.2) * mm});
            skLineSegment(sketch, "E445", {"start": v(14.07, 11.2) * mm, "end": v(13.97, 11.22) * mm});
            skLineSegment(sketch, "E446", {"start": v(13.97, 11.22) * mm, "end": v(9.55, 10.53) * mm});
            skLineSegment(sketch, "E447", {"start": v(9.55, 10.53) * mm, "end": v(9.44, 10.4) * mm});
            skLineSegment(sketch, "E448", {"start": v(9.44, 10.4) * mm, "end": v(9.44, -6.8) * mm});
            skLineSegment(sketch, "E449", {"start": v(9.44, -6.8) * mm, "end": v(9.58, -6.94) * mm});
            skLineSegment(sketch, "E450", {"start": v(9.58, -6.94) * mm, "end": v(14, -6.94) * mm});
            skLineSegment(sketch, "E451", {"start": v(14, -6.94) * mm, "end": v(14.13, -6.8) * mm});
            skLineSegment(sketch, "E452", {"start": v(14.13, -6.8) * mm, "end": v(14.13, 1.06) * mm});
            skLineSegment(sketch, "E453", {"start": v(14.13, 1.06) * mm, "end": v(14.82, 1.57) * mm});
            skLineSegment(sketch, "E454", {"start": v(14.82, 1.57) * mm, "end": v(15.45, 1.73) * mm});
            skLineSegment(sketch, "E455", {"start": v(15.45, 1.73) * mm, "end": v(15.9, 1.62) * mm});
            skLineSegment(sketch, "E456", {"start": v(15.9, 1.62) * mm, "end": v(16.18, 1.36) * mm});
            skLineSegment(sketch, "E457", {"start": v(16.18, 1.36) * mm, "end": v(16.3, 1) * mm});
            skLineSegment(sketch, "E458", {"start": v(16.3, 1) * mm, "end": v(16.34, 0.62) * mm});
            skLineSegment(sketch, "E459", {"start": v(16.34, 0.62) * mm, "end": v(16.34, -6.78) * mm});
            skLineSegment(sketch, "E460", {"start": v(16.34, -6.78) * mm, "end": v(16.48, -6.91) * mm});
            skLineSegment(sketch, "E461", {"start": v(16.48, -6.91) * mm, "end": v(20.9, -6.91) * mm});
            skLineSegment(sketch, "E462", {"start": v(20.9, -6.91) * mm, "end": v(21.03, -6.78) * mm});
            skLineSegment(sketch, "E463", {"start": v(21.03, -6.78) * mm, "end": v(21.03, 1.86) * mm});
            skLineSegment(sketch, "E464", {"start": v(21.03, 1.86) * mm, "end": v(20.8, 3.57) * mm});
            skLineSegment(sketch, "E465", {"start": v(20.8, 3.57) * mm, "end": v(20.1, 4.81) * mm});
            skLineSegment(sketch, "E466", {"start": v(20.1, 4.81) * mm, "end": v(18.98, 5.58) * mm});
            skLineSegment(sketch, "E467", {"start": v(18.98, 5.58) * mm, "end": v(17.44, 5.84) * mm});
            skLineSegment(sketch, "E468", {"start": v(30.52, -3.05) * mm, "end": v(30.47, -2.97) * mm});
            skLineSegment(sketch, "E469", {"start": v(30.47, -2.97) * mm, "end": v(30.36, -2.97) * mm});
            skLineSegment(sketch, "E470", {"start": v(30.36, -2.97) * mm, "end": v(29.56, -3.1) * mm});
            skLineSegment(sketch, "E471", {"start": v(29.56, -3.1) * mm, "end": v(28.97, -3.03) * mm});
            skLineSegment(sketch, "E472", {"start": v(28.97, -3.03) * mm, "end": v(28.57, -2.8) * mm});
            skLineSegment(sketch, "E473", {"start": v(28.57, -2.8) * mm, "end": v(28.33, -2.4) * mm});
            skLineSegment(sketch, "E474", {"start": v(28.33, -2.4) * mm, "end": v(28.26, -1.83) * mm});
            skLineSegment(sketch, "E475", {"start": v(28.26, -1.83) * mm, "end": v(28.26, 1.8) * mm});
            skLineSegment(sketch, "E476", {"start": v(28.26, 1.8) * mm, "end": v(30.58, 1.8) * mm});
            skLineSegment(sketch, "E477", {"start": v(30.58, 1.8) * mm, "end": v(30.72, 1.95) * mm});
            skLineSegment(sketch, "E478", {"start": v(30.72, 1.95) * mm, "end": v(30.72, 6.03) * mm});
            skLineSegment(sketch, "E479", {"start": v(30.72, 6.03) * mm, "end": v(30.66, 6.14) * mm});
            skLineSegment(sketch, "E480", {"start": v(30.66, 6.14) * mm, "end": v(30.55, 6.17) * mm});
            skLineSegment(sketch, "E481", {"start": v(30.55, 6.17) * mm, "end": v(28.23, 5.64) * mm});
            skLineSegment(sketch, "E482", {"start": v(28.23, 5.64) * mm, "end": v(28.23, 9.67) * mm});
            skLineSegment(sketch, "E483", {"start": v(28.23, 9.67) * mm, "end": v(28.18, 9.76) * mm});
            skLineSegment(sketch, "E484", {"start": v(28.18, 9.76) * mm, "end": v(28.07, 9.78) * mm});
            skLineSegment(sketch, "E485", {"start": v(28.07, 9.78) * mm, "end": v(23.68, 9.1) * mm});
            skLineSegment(sketch, "E486", {"start": v(23.68, 9.1) * mm, "end": v(23.57, 8.96) * mm});
            skLineSegment(sketch, "E487", {"start": v(23.57, 8.96) * mm, "end": v(23.57, 4.87) * mm});
            skLineSegment(sketch, "E488", {"start": v(23.57, 4.87) * mm, "end": v(22.13, 4.51) * mm});
            skLineSegment(sketch, "E489", {"start": v(22.13, 4.51) * mm, "end": v(22.05, 4.4) * mm});
            skLineSegment(sketch, "E490", {"start": v(22.05, 4.4) * mm, "end": v(22.05, 1.92) * mm});
            skLineSegment(sketch, "E491", {"start": v(22.05, 1.92) * mm, "end": v(22.19, 1.78) * mm});
            skLineSegment(sketch, "E492", {"start": v(22.19, 1.78) * mm, "end": v(23.6, 1.78) * mm});
            skLineSegment(sketch, "E493", {"start": v(23.6, 1.78) * mm, "end": v(23.6, -2.52) * mm});
            skLineSegment(sketch, "E494", {"start": v(23.6, -2.52) * mm, "end": v(23.9, -4.53) * mm});
            skLineSegment(sketch, "E495", {"start": v(23.9, -4.53) * mm, "end": v(24.83, -5.95) * mm});
            skLineSegment(sketch, "E496", {"start": v(24.83, -5.95) * mm, "end": v(26.38, -6.8) * mm});
            skLineSegment(sketch, "E497", {"start": v(26.38, -6.8) * mm, "end": v(28.56, -7.08) * mm});
            skLineSegment(sketch, "E498", {"start": v(28.56, -7.08) * mm, "end": v(29.9, -7) * mm});
            skLineSegment(sketch, "E499", {"start": v(29.9, -7) * mm, "end": v(31.21, -6.7) * mm});
            skLineSegment(sketch, "E500", {"start": v(31.21, -6.7) * mm, "end": v(31.3, -6.55) * mm});
            skLineSegment(sketch, "E501", {"start": v(31.3, -6.55) * mm, "end": v(30.52, -3.05) * mm});
            skLineSegment(sketch, "E502", {"start": v(38.17, -4.76) * mm, "end": v(38, -5.6) * mm});
            skLineSegment(sketch, "E503", {"start": v(38, -5.6) * mm, "end": v(37.54, -6.28) * mm});
            skLineSegment(sketch, "E504", {"start": v(37.54, -6.28) * mm, "end": v(36.85, -6.74) * mm});
            skLineSegment(sketch, "E505", {"start": v(36.85, -6.74) * mm, "end": v(36.02, -6.91) * mm});
            skLineSegment(sketch, "E506", {"start": v(36.02, -6.91) * mm, "end": v(35.18, -6.74) * mm});
            skLineSegment(sketch, "E507", {"start": v(35.18, -6.74) * mm, "end": v(34.5, -6.28) * mm});
            skLineSegment(sketch, "E508", {"start": v(34.5, -6.28) * mm, "end": v(34.03, -5.6) * mm});
            skLineSegment(sketch, "E509", {"start": v(34.03, -5.6) * mm, "end": v(33.86, -4.76) * mm});
            skLineSegment(sketch, "E510", {"start": v(33.86, -4.76) * mm, "end": v(34.03, -3.92) * mm});
            skLineSegment(sketch, "E511", {"start": v(34.03, -3.92) * mm, "end": v(34.5, -3.24) * mm});
            skLineSegment(sketch, "E512", {"start": v(34.5, -3.24) * mm, "end": v(35.18, -2.78) * mm});
            skLineSegment(sketch, "E513", {"start": v(35.18, -2.78) * mm, "end": v(36.02, -2.6) * mm});
            skLineSegment(sketch, "E514", {"start": v(36.02, -2.6) * mm, "end": v(36.85, -2.78) * mm});
            skLineSegment(sketch, "E515", {"start": v(36.85, -2.78) * mm, "end": v(37.54, -3.24) * mm});
            skLineSegment(sketch, "E516", {"start": v(37.54, -3.24) * mm, "end": v(38, -3.92) * mm});
            skLineSegment(sketch, "E517", {"start": v(38, -3.92) * mm, "end": v(38.17, -4.76) * mm});
            skSolve(sketch);
        }
        {
            var Q0;
            Q0=makeQuery(id+"F2.imprint","IMPRINT",FACE,{"disambiguationData":[TD([[makeQuery(id+"F2.imprint","IMPRINT",EDGE,{"derivedFrom":sQuery(id+"F2.wireOp",EDGE,"E263")}),1.0]])]});
            var Q1;
            Q1=makeQuery(id+"F2.imprint","IMPRINT",FACE,{"disambiguationData":[TD([[makeQuery(id+"F2.imprint","IMPRINT",EDGE,{"derivedFrom":sQuery(id+"F2.wireOp",EDGE,"E300")}),1.0]])]});
            var Q2;
            Q2=makeQuery(id+"F2.imprint","IMPRINT",FACE,{"disambiguationData":[TD([[makeQuery(id+"F2.imprint","IMPRINT",EDGE,{"derivedFrom":sQuery(id+"F2.wireOp",EDGE,"E344")}),1.0]])]});
            var Q3;
            Q3=makeQuery(id+"F2.imprint","IMPRINT",FACE,{"disambiguationData":[TD([[makeQuery(id+"F2.imprint","IMPRINT",EDGE,{"derivedFrom":sQuery(id+"F2.wireOp",EDGE,"E328")}),1.0]])]});
            var Q4;
            Q4=makeQuery(id+"F2.imprint","IMPRINT",FACE,{"disambiguationData":[TD([[makeQuery(id+"F2.imprint","IMPRINT",EDGE,{"derivedFrom":sQuery(id+"F2.wireOp",EDGE,"E352")}),1.0]])]});
            var Q5;
            Q5=makeQuery(id+"F2.imprint","IMPRINT",FACE,{"disambiguationData":[TD([[makeQuery(id+"F2.imprint","IMPRINT",EDGE,{"derivedFrom":sQuery(id+"F2.wireOp",EDGE,"E439")}),1.0]])]});
            var Q6;
            Q6=makeQuery(id+"F2.imprint","IMPRINT",FACE,{"disambiguationData":[TD([[makeQuery(id+"F2.imprint","IMPRINT",EDGE,{"derivedFrom":sQuery(id+"F2.wireOp",EDGE,"E468")}),1.0]])]});
            var Q7;
            Q7=makeQuery(id+"F2.imprint","IMPRINT",FACE,{"disambiguationData":[TD([[makeQuery(id+"F2.imprint","IMPRINT",EDGE,{"derivedFrom":sQuery(id+"F2.wireOp",EDGE,"E502")}),-1.0]])]});
            extrude(context, id + "F3", {"entities" : qUnion([Q0, Q1, Q2, Q3, Q4, Q5, Q6, Q7]), "operationType" : NewBodyOperationType.REMOVE, "oppositeDirection" : true, "depth" : 4 * mm});
        }
        {
            var Q0;
            {var subQ0=sQuery(id+"F0.wireOp",EDGE,"E0");var subQ1=sQuery(id+"F0.wireOp",EDGE,"E1");var subQ2=sQuery(id+"F0.wireOp",EDGE,"E2");var subQ3=sQuery(id+"F0.wireOp",EDGE,"E3");var subQ4=sQuery(id+"F0.wireOp",EDGE,"E4");var subQ5=sQuery(id+"F0.wireOp",EDGE,"E5");var subQ6=sQuery(id+"F0.wireOp",EDGE,"E6");var subQ7=sQuery(id+"F0.wireOp",EDGE,"E7");var subQ8=sQuery(id+"F0.wireOp",EDGE,"E8");var subQ9=sQuery(id+"F0.wireOp",EDGE,"E9");var subQ10=sQuery(id+"F0.wireOp",EDGE,"E10");var subQ11=sQuery(id+"F0.wireOp",EDGE,"E11");var subQ12=sQuery(id+"F0.wireOp",EDGE,"E12");var subQ13=sQuery(id+"F0.wireOp",EDGE,"E13");var subQ14=sQuery(id+"F0.wireOp",EDGE,"E14");var subQ15=sQuery(id+"F0.wireOp",EDGE,"E15");var subQ16=sQuery(id+"F0.wireOp",EDGE,"E16");var subQ17=sQuery(id+"F0.wireOp",EDGE,"E17");var subQ18=sQuery(id+"F0.wireOp",EDGE,"E18");var subQ19=sQuery(id+"F0.wireOp",EDGE,"E19");var subQ20=sQuery(id+"F0.wireOp",EDGE,"E20");var subQ21=sQuery(id+"F0.wireOp",EDGE,"E21");var subQ22=sQuery(id+"F0.wireOp",EDGE,"E22");var subQ23=sQuery(id+"F0.wireOp",EDGE,"E34");var subQ24=sQuery(id+"F0.wireOp",EDGE,"E35");var subQ25=sQuery(id+"F0.wireOp",EDGE,"E36");var subQ26=sQuery(id+"F0.wireOp",EDGE,"E37");var subQ27=sQuery(id+"F0.wireOp",EDGE,"E38");var subQ28=sQuery(id+"F0.wireOp",EDGE,"E39");var subQ29=sQuery(id+"F0.wireOp",EDGE,"E40");var subQ30=sQuery(id+"F0.wireOp",EDGE,"E41");var subQ31=sQuery(id+"F0.wireOp",EDGE,"E50");var subQ32=sQuery(id+"F0.wireOp",EDGE,"E51");var subQ33=sQuery(id+"F0.wireOp",EDGE,"E52");var subQ34=sQuery(id+"F0.wireOp",EDGE,"E53");var subQ35=sQuery(id+"F0.wireOp",EDGE,"E54");var subQ36=sQuery(id+"F0.wireOp",EDGE,"E55");var subQ37=sQuery(id+"F0.wireOp",EDGE,"E63");var subQ38=sQuery(id+"F0.wireOp",EDGE,"E64");var subQ39=sQuery(id+"F0.wireOp",EDGE,"E65");var subQ40=sQuery(id+"F0.wireOp",EDGE,"E66");var subQ41=sQuery(id+"F0.wireOp",EDGE,"E67");var subQ42=sQuery(id+"F0.wireOp",EDGE,"E68");var subQ43=sQuery(id+"F0.wireOp",EDGE,"E69");var subQ44=sQuery(id+"F0.wireOp",EDGE,"E70");var subQ45=sQuery(id+"F0.wireOp",EDGE,"E71");var subQ46=sQuery(id+"F0.wireOp",EDGE,"E72");var subQ47=sQuery(id+"F0.wireOp",EDGE,"E87");var subQ48=sQuery(id+"F0.wireOp",EDGE,"E88");var subQ49=sQuery(id+"F0.wireOp",EDGE,"E89");var subQ50=sQuery(id+"F0.wireOp",EDGE,"E90");var subQ51=sQuery(id+"F0.wireOp",EDGE,"E91");var subQ52=sQuery(id+"F0.wireOp",EDGE,"E92");var subQ53=sQuery(id+"F0.wireOp",EDGE,"E93");var subQ54=sQuery(id+"F0.wireOp",EDGE,"E94");var subQ55=sQuery(id+"F0.wireOp",EDGE,"E95");var subQ56=sQuery(id+"F0.wireOp",EDGE,"E105");var subQ57=sQuery(id+"F0.wireOp",EDGE,"E106");var subQ58=sQuery(id+"F0.wireOp",EDGE,"E117");var subQ59=sQuery(id+"F0.wireOp",EDGE,"E118");var subQ60=sQuery(id+"F0.wireOp",EDGE,"E119");var subQ61=sQuery(id+"F0.wireOp",EDGE,"E120");var subQ62=sQuery(id+"F0.wireOp",EDGE,"E121");var subQ63=sQuery(id+"F0.wireOp",EDGE,"E132");var subQ64=sQuery(id+"F0.wireOp",EDGE,"E133");var subQ65=sQuery(id+"F0.wireOp",EDGE,"E134");var subQ66=sQuery(id+"F0.wireOp",EDGE,"E135");var subQ67=sQuery(id+"F0.wireOp",EDGE,"E136");var subQ68=sQuery(id+"F0.wireOp",EDGE,"E137");var subQ69=sQuery(id+"F0.wireOp",EDGE,"E138");var subQ70=sQuery(id+"F0.wireOp",EDGE,"E139");var subQ71=sQuery(id+"F0.wireOp",EDGE,"E140");var subQ72=sQuery(id+"F0.wireOp",EDGE,"E141");var subQ73=sQuery(id+"F0.wireOp",EDGE,"E157");var subQ74=sQuery(id+"F0.wireOp",EDGE,"E158");var subQ75=sQuery(id+"F0.wireOp",EDGE,"E159");var subQ76=sQuery(id+"F0.wireOp",EDGE,"E160");var subQ77=sQuery(id+"F0.wireOp",EDGE,"E161");var subQ78=sQuery(id+"F0.wireOp",EDGE,"E162");var subQ79=sQuery(id+"F0.wireOp",EDGE,"E163");var subQ80=sQuery(id+"F0.wireOp",EDGE,"E164");var subQ81=sQuery(id+"F0.wireOp",EDGE,"E169");var subQ82=sQuery(id+"F0.wireOp",EDGE,"E170");var subQ83=sQuery(id+"F0.wireOp",EDGE,"E171");var subQ84=sQuery(id+"F0.wireOp",EDGE,"E172");var subQ85=sQuery(id+"F0.wireOp",EDGE,"E173");var subQ86=sQuery(id+"F0.wireOp",EDGE,"E174");var subQ87=sQuery(id+"F0.wireOp",EDGE,"E175");var subQ88=sQuery(id+"F0.wireOp",EDGE,"E180");var subQ89=sQuery(id+"F0.wireOp",EDGE,"E181");var subQ90=sQuery(id+"F0.wireOp",EDGE,"E182");var subQ91=sQuery(id+"F0.wireOp",EDGE,"E183");var subQ92=sQuery(id+"F0.wireOp",EDGE,"E184");var subQ93=sQuery(id+"F0.wireOp",EDGE,"E185");var subQ94=sQuery(id+"F0.wireOp",EDGE,"E186");var subQ95=sQuery(id+"F0.wireOp",EDGE,"E187");var subQ96=sQuery(id+"F0.wireOp",EDGE,"E188");var subQ97=sQuery(id+"F0.wireOp",EDGE,"E189");var subQ98=sQuery(id+"F0.wireOp",EDGE,"E190");var subQ99=sQuery(id+"F0.wireOp",EDGE,"E191");var subQ100=sQuery(id+"F0.wireOp",EDGE,"E192");var subQ101=sQuery(id+"F0.wireOp",EDGE,"E193");var subQ102=sQuery(id+"F0.wireOp",EDGE,"E194");var subQ103=sQuery(id+"F0.wireOp",EDGE,"E195");var subQ104=sQuery(id+"F0.wireOp",EDGE,"E196");var subQ105=sQuery(id+"F0.wireOp",EDGE,"E209");var subQ106=sQuery(id+"F0.wireOp",EDGE,"E210");var subQ107=sQuery(id+"F0.wireOp",EDGE,"E211");var subQ108=sQuery(id+"F0.wireOp",EDGE,"E212");var subQ109=sQuery(id+"F0.wireOp",EDGE,"E213");var subQ110=sQuery(id+"F0.wireOp",EDGE,"E219");var subQ111=sQuery(id+"F0.wireOp",EDGE,"E220");var subQ112=sQuery(id+"F0.wireOp",EDGE,"E221");var subQ113=sQuery(id+"F0.wireOp",EDGE,"E222");var subQ114=sQuery(id+"F0.wireOp",EDGE,"E223");var subQ115=sQuery(id+"F0.wireOp",EDGE,"E224");var subQ116=sQuery(id+"F0.wireOp",EDGE,"E225");var subQ117=sQuery(id+"F0.wireOp",EDGE,"E226");var subQ118=sQuery(id+"F0.wireOp",EDGE,"E227");var subQ119=sQuery(id+"F0.wireOp",EDGE,"E228");var subQ120=sQuery(id+"F0.wireOp",EDGE,"E229");var subQ121=sQuery(id+"F0.wireOp",EDGE,"E230");var subQ122=sQuery(id+"F0.wireOp",EDGE,"E231");var subQ123=sQuery(id+"F0.wireOp",EDGE,"E232");var subQ124=sQuery(id+"F0.wireOp",EDGE,"E233");var subQ125=sQuery(id+"F0.wireOp",EDGE,"E234");var subQ126=sQuery(id+"F0.wireOp",EDGE,"E243");var subQ127=sQuery(id+"F0.wireOp",EDGE,"E244");var subQ128=sQuery(id+"F0.wireOp",EDGE,"E245");var subQ129=sQuery(id+"F0.wireOp",EDGE,"E246");var subQ130=sQuery(id+"F0.wireOp",EDGE,"E247");var subQ131=sQuery(id+"F0.wireOp",EDGE,"E248");var subQ132=sQuery(id+"F0.wireOp",EDGE,"E249");var subQ133=sQuery(id+"F0.wireOp",EDGE,"E250");var subQ134=sQuery(id+"F0.wireOp",EDGE,"E251");var subQ135=sQuery(id+"F0.wireOp",EDGE,"E252");var subQ136=sQuery(id+"F0.wireOp",EDGE,"E253");var subQ137=sQuery(id+"F0.wireOp",EDGE,"E254");var subQ138=sQuery(id+"F0.wireOp",EDGE,"E255");var subQ139=sQuery(id+"F0.wireOp",EDGE,"E256");var subQ140=sQuery(id+"F0.wireOp",EDGE,"E257");var subQ141=sQuery(id+"F0.wireOp",EDGE,"E258");var subQ142=sQuery(id+"F0.wireOp",EDGE,"E259");var subQ143=sQuery(id+"F0.wireOp",EDGE,"E260");var subQ144=sQuery(id+"F0.wireOp",EDGE,"E261");var subQ145=sQuery(id+"F0.wireOp",EDGE,"E262");Q0=makeQuery(id+"F3.boolean.opBoolean","SPLIT",FACE,{"disambiguationData":[TD([makeQuery(id+"F1.opExtrude","SWEPT_FACE",FACE,{"disambiguationData":[OSD([subQ0])]})])],"derivedFrom":makeQuery(id+"F1.opExtrude","CAP_FACE",FACE,{"disambiguationData":[OSD([subQ0,subQ1,subQ2,subQ3,subQ4,subQ5,subQ6,subQ7,subQ8,subQ9,subQ10,subQ11,subQ12,subQ13,subQ14,subQ15,subQ16,subQ17,subQ18,subQ19,subQ20,subQ21,subQ22,subQ23,subQ24,subQ25,subQ26,subQ27,subQ28,subQ29,subQ30,subQ31,subQ32,subQ33,subQ34,subQ35,subQ36,subQ37,subQ38,subQ39,subQ40,subQ41,subQ42,subQ43,subQ44,subQ45,subQ46,subQ47,subQ48,subQ49,subQ50,subQ51,subQ52,subQ53,subQ54,subQ55,subQ56,subQ57,subQ58,subQ59,subQ60,subQ61,subQ62,subQ63,subQ64,subQ65,subQ66,subQ67,subQ68,subQ69,subQ70,subQ71,subQ72,subQ73,subQ74,subQ75,subQ76,subQ77,subQ78,subQ79,subQ80,subQ81,subQ82,subQ83,subQ84,subQ85,subQ86,subQ87,subQ88,subQ89,subQ90,subQ91,subQ92,subQ93,subQ94,subQ95,subQ96,subQ97,subQ98,subQ99,subQ100,subQ101,subQ102,subQ103,subQ104,subQ105,subQ106,subQ107,subQ108,subQ109,subQ110,subQ111,subQ112,subQ113,subQ114,subQ115,subQ116,subQ117,subQ118,subQ119,subQ120,subQ121,subQ122,subQ123,subQ124,subQ125,subQ126,subQ127,subQ128,subQ129,subQ130,subQ131,subQ132,subQ133,subQ134,subQ135,subQ136,subQ137,subQ138,subQ139,subQ140,subQ141,subQ142,subQ143,subQ144,subQ145])],"isStart":false})});}
            var sketch = newSketch(context, id + "F4", { "sketchPlane" : qUnion([Q0])});
            skLineSegment(sketch, "E518.bottom", {"start": v(-43.19, 17.12) * mm, "end": v(43.08, 17.12) * mm});
            skLineSegment(sketch, "E518.top", {"start": v(-43.19, -15.8) * mm, "end": v(43.08, -15.8) * mm});
            skLineSegment(sketch, "E518.left", {"start": v(-43.19, 17.12) * mm, "end": v(-43.19, -15.8) * mm});
            skLineSegment(sketch, "E518.right", {"start": v(43.08, 17.12) * mm, "end": v(43.08, -15.8) * mm});
            skSolve(sketch);
        }
        {
            var Q0;
            Q0=makeQuery(id+"F4.imprint","IMPRINT",FACE,{"disambiguationData":[TD([[makeQuery(id+"F4.imprint","IMPRINT",EDGE,{"derivedFrom":makeQuery(id+"F3.boolean.opBoolean","COPY",EDGE,{"derivedFrom":makeQuery(id+"F3.opExtrude","CAP_EDGE",EDGE,{"disambiguationData":[OSD([sQuery(id+"F2.wireOp",EDGE,"E263")])],"isStart":true})})}),1.0]])]});
            var Q1;
            Q1=makeQuery(id+"F4.imprint","IMPRINT",FACE,{"disambiguationData":[TD([[makeQuery(id+"F4.imprint","IMPRINT",EDGE,{"derivedFrom":makeQuery(id+"F1.opExtrude","CAP_EDGE",EDGE,{"disambiguationData":[OSD([sQuery(id+"F0.wireOp",EDGE,"E0")])],"isStart":false})}),1.0]])]});
            var Q2;
            Q2=makeQuery(id+"F4.imprint","IMPRINT",FACE,{"disambiguationData":[TD([[makeQuery(id+"F4.imprint","IMPRINT",EDGE,{"derivedFrom":makeQuery(id+"F3.boolean.opBoolean","COPY",EDGE,{"derivedFrom":makeQuery(id+"F3.opExtrude","CAP_EDGE",EDGE,{"disambiguationData":[OSD([sQuery(id+"F2.wireOp",EDGE,"E300")])],"isStart":true})})}),1.0]])]});
            var Q3;
            Q3=makeQuery(id+"F4.imprint","IMPRINT",FACE,{"disambiguationData":[TD([[makeQuery(id+"F4.imprint","IMPRINT",EDGE,{"derivedFrom":makeQuery(id+"F3.boolean.opBoolean","COPY",EDGE,{"derivedFrom":makeQuery(id+"F3.opExtrude","CAP_EDGE",EDGE,{"disambiguationData":[OSD([sQuery(id+"F2.wireOp",EDGE,"E344")])],"isStart":true})})}),1.0]])]});
            var Q4;
            Q4=makeQuery(id+"F4.imprint","IMPRINT",FACE,{"disambiguationData":[TD([[makeQuery(id+"F4.imprint","IMPRINT",EDGE,{"derivedFrom":makeQuery(id+"F3.boolean.opBoolean","COPY",EDGE,{"derivedFrom":makeQuery(id+"F3.opExtrude","CAP_EDGE",EDGE,{"disambiguationData":[OSD([sQuery(id+"F2.wireOp",EDGE,"E328")])],"isStart":true})})}),1.0]])]});
            var Q5;
            Q5=makeQuery(id+"F4.imprint","IMPRINT",FACE,{"disambiguationData":[TD([[makeQuery(id+"F4.imprint","IMPRINT",EDGE,{"derivedFrom":makeQuery(id+"F3.boolean.opBoolean","COPY",EDGE,{"derivedFrom":makeQuery(id+"F3.opExtrude","CAP_EDGE",EDGE,{"disambiguationData":[OSD([sQuery(id+"F2.wireOp",EDGE,"E352")])],"isStart":true})})}),1.0]])]});
            var Q6;
            Q6=makeQuery(id+"F4.imprint","IMPRINT",FACE,{"disambiguationData":[TD([[makeQuery(id+"F4.imprint","IMPRINT",EDGE,{"derivedFrom":makeQuery(id+"F3.boolean.opBoolean","COPY",EDGE,{"derivedFrom":makeQuery(id+"F3.opExtrude","CAP_EDGE",EDGE,{"disambiguationData":[OSD([sQuery(id+"F2.wireOp",EDGE,"E439")])],"isStart":true})})}),1.0]])]});
            var Q7;
            Q7=makeQuery(id+"F4.imprint","IMPRINT",FACE,{"disambiguationData":[TD([[makeQuery(id+"F4.imprint","IMPRINT",EDGE,{"derivedFrom":makeQuery(id+"F3.boolean.opBoolean","COPY",EDGE,{"derivedFrom":makeQuery(id+"F3.opExtrude","CAP_EDGE",EDGE,{"disambiguationData":[OSD([sQuery(id+"F2.wireOp",EDGE,"E468")])],"isStart":true})})}),1.0]])]});
            var Q8;
            Q8=makeQuery(id+"F4.imprint","IMPRINT",FACE,{"disambiguationData":[TD([[makeQuery(id+"F4.imprint","IMPRINT",EDGE,{"derivedFrom":makeQuery(id+"F3.boolean.opBoolean","COPY",EDGE,{"derivedFrom":makeQuery(id+"F3.opExtrude","CAP_EDGE",EDGE,{"disambiguationData":[OSD([sQuery(id+"F2.wireOp",EDGE,"E502")])],"isStart":true})})}),-1.0]])]});
            extrude(context, id + "F5", {"entities" : qUnion([Q0, Q1, Q2, Q3, Q4, Q5, Q6, Q7, Q8]), "operationType" : NewBodyOperationType.ADD, "depth" : 1 * mm});
        }
        {
            var Q0;
            Q0=makeQuery(id+"F5.opExtrude","CAP_FACE",FACE,{"disambiguationData":[OSD([sQuery(id+"F0.wireOp",EDGE,"E0"),sQuery(id+"F0.wireOp",EDGE,"E1"),sQuery(id+"F0.wireOp",EDGE,"E2"),sQuery(id+"F0.wireOp",EDGE,"E3"),sQuery(id+"F0.wireOp",EDGE,"E4"),sQuery(id+"F0.wireOp",EDGE,"E5"),sQuery(id+"F0.wireOp",EDGE,"E6"),sQuery(id+"F0.wireOp",EDGE,"E7"),sQuery(id+"F0.wireOp",EDGE,"E8"),sQuery(id+"F0.wireOp",EDGE,"E9"),sQuery(id+"F0.wireOp",EDGE,"E10"),sQuery(id+"F0.wireOp",EDGE,"E11"),sQuery(id+"F0.wireOp",EDGE,"E12"),sQuery(id+"F0.wireOp",EDGE,"E13"),sQuery(id+"F0.wireOp",EDGE,"E14"),sQuery(id+"F0.wireOp",EDGE,"E15"),sQuery(id+"F0.wireOp",EDGE,"E16"),sQuery(id+"F0.wireOp",EDGE,"E17"),sQuery(id+"F0.wireOp",EDGE,"E18"),sQuery(id+"F0.wireOp",EDGE,"E19"),sQuery(id+"F0.wireOp",EDGE,"E20"),sQuery(id+"F0.wireOp",EDGE,"E21"),sQuery(id+"F0.wireOp",EDGE,"E22"),sQuery(id+"F0.wireOp",EDGE,"E34"),sQuery(id+"F0.wireOp",EDGE,"E35"),sQuery(id+"F0.wireOp",EDGE,"E36"),sQuery(id+"F0.wireOp",EDGE,"E37"),sQuery(id+"F0.wireOp",EDGE,"E38"),sQuery(id+"F0.wireOp",EDGE,"E39"),sQuery(id+"F0.wireOp",EDGE,"E40"),sQuery(id+"F0.wireOp",EDGE,"E41"),sQuery(id+"F0.wireOp",EDGE,"E50"),sQuery(id+"F0.wireOp",EDGE,"E51"),sQuery(id+"F0.wireOp",EDGE,"E52"),sQuery(id+"F0.wireOp",EDGE,"E53"),sQuery(id+"F0.wireOp",EDGE,"E54"),sQuery(id+"F0.wireOp",EDGE,"E55"),sQuery(id+"F0.wireOp",EDGE,"E63"),sQuery(id+"F0.wireOp",EDGE,"E64"),sQuery(id+"F0.wireOp",EDGE,"E65"),sQuery(id+"F0.wireOp",EDGE,"E66"),sQuery(id+"F0.wireOp",EDGE,"E67"),sQuery(id+"F0.wireOp",EDGE,"E68"),sQuery(id+"F0.wireOp",EDGE,"E69"),sQuery(id+"F0.wireOp",EDGE,"E70"),sQuery(id+"F0.wireOp",EDGE,"E71"),sQuery(id+"F0.wireOp",EDGE,"E72"),sQuery(id+"F0.wireOp",EDGE,"E87"),sQuery(id+"F0.wireOp",EDGE,"E88"),sQuery(id+"F0.wireOp",EDGE,"E89"),sQuery(id+"F0.wireOp",EDGE,"E90"),sQuery(id+"F0.wireOp",EDGE,"E91"),sQuery(id+"F0.wireOp",EDGE,"E92"),sQuery(id+"F0.wireOp",EDGE,"E93"),sQuery(id+"F0.wireOp",EDGE,"E94"),sQuery(id+"F0.wireOp",EDGE,"E95"),sQuery(id+"F0.wireOp",EDGE,"E105"),sQuery(id+"F0.wireOp",EDGE,"E106"),sQuery(id+"F0.wireOp",EDGE,"E117"),sQuery(id+"F0.wireOp",EDGE,"E118"),sQuery(id+"F0.wireOp",EDGE,"E119"),sQuery(id+"F0.wireOp",EDGE,"E120"),sQuery(id+"F0.wireOp",EDGE,"E121"),sQuery(id+"F0.wireOp",EDGE,"E132"),sQuery(id+"F0.wireOp",EDGE,"E133"),sQuery(id+"F0.wireOp",EDGE,"E134"),sQuery(id+"F0.wireOp",EDGE,"E135"),sQuery(id+"F0.wireOp",EDGE,"E136"),sQuery(id+"F0.wireOp",EDGE,"E137"),sQuery(id+"F0.wireOp",EDGE,"E138"),sQuery(id+"F0.wireOp",EDGE,"E139"),sQuery(id+"F0.wireOp",EDGE,"E140"),sQuery(id+"F0.wireOp",EDGE,"E141"),sQuery(id+"F0.wireOp",EDGE,"E157"),sQuery(id+"F0.wireOp",EDGE,"E158"),sQuery(id+"F0.wireOp",EDGE,"E159"),sQuery(id+"F0.wireOp",EDGE,"E160"),sQuery(id+"F0.wireOp",EDGE,"E161"),sQuery(id+"F0.wireOp",EDGE,"E162"),sQuery(id+"F0.wireOp",EDGE,"E163"),sQuery(id+"F0.wireOp",EDGE,"E164"),sQuery(id+"F0.wireOp",EDGE,"E169"),sQuery(id+"F0.wireOp",EDGE,"E170"),sQuery(id+"F0.wireOp",EDGE,"E171"),sQuery(id+"F0.wireOp",EDGE,"E172"),sQuery(id+"F0.wireOp",EDGE,"E173"),sQuery(id+"F0.wireOp",EDGE,"E174"),sQuery(id+"F0.wireOp",EDGE,"E175"),sQuery(id+"F0.wireOp",EDGE,"E180"),sQuery(id+"F0.wireOp",EDGE,"E181"),sQuery(id+"F0.wireOp",EDGE,"E182"),sQuery(id+"F0.wireOp",EDGE,"E183"),sQuery(id+"F0.wireOp",EDGE,"E184"),sQuery(id+"F0.wireOp",EDGE,"E185"),sQuery(id+"F0.wireOp",EDGE,"E186"),sQuery(id+"F0.wireOp",EDGE,"E187"),sQuery(id+"F0.wireOp",EDGE,"E188"),sQuery(id+"F0.wireOp",EDGE,"E189"),sQuery(id+"F0.wireOp",EDGE,"E190"),sQuery(id+"F0.wireOp",EDGE,"E191"),sQuery(id+"F0.wireOp",EDGE,"E192"),sQuery(id+"F0.wireOp",EDGE,"E193"),sQuery(id+"F0.wireOp",EDGE,"E194"),sQuery(id+"F0.wireOp",EDGE,"E195"),sQuery(id+"F0.wireOp",EDGE,"E196"),sQuery(id+"F0.wireOp",EDGE,"E209"),sQuery(id+"F0.wireOp",EDGE,"E210"),sQuery(id+"F0.wireOp",EDGE,"E211"),sQuery(id+"F0.wireOp",EDGE,"E212"),sQuery(id+"F0.wireOp",EDGE,"E213"),sQuery(id+"F0.wireOp",EDGE,"E219"),sQuery(id+"F0.wireOp",EDGE,"E220"),sQuery(id+"F0.wireOp",EDGE,"E221"),sQuery(id+"F0.wireOp",EDGE,"E222"),sQuery(id+"F0.wireOp",EDGE,"E223"),sQuery(id+"F0.wireOp",EDGE,"E224"),sQuery(id+"F0.wireOp",EDGE,"E225"),sQuery(id+"F0.wireOp",EDGE,"E226"),sQuery(id+"F0.wireOp",EDGE,"E227"),sQuery(id+"F0.wireOp",EDGE,"E228"),sQuery(id+"F0.wireOp",EDGE,"E229"),sQuery(id+"F0.wireOp",EDGE,"E230"),sQuery(id+"F0.wireOp",EDGE,"E231"),sQuery(id+"F0.wireOp",EDGE,"E232"),sQuery(id+"F0.wireOp",EDGE,"E233"),sQuery(id+"F0.wireOp",EDGE,"E234"),sQuery(id+"F0.wireOp",EDGE,"E243"),sQuery(id+"F0.wireOp",EDGE,"E244"),sQuery(id+"F0.wireOp",EDGE,"E245"),sQuery(id+"F0.wireOp",EDGE,"E246"),sQuery(id+"F0.wireOp",EDGE,"E247"),sQuery(id+"F0.wireOp",EDGE,"E248"),sQuery(id+"F0.wireOp",EDGE,"E249"),sQuery(id+"F0.wireOp",EDGE,"E250"),sQuery(id+"F0.wireOp",EDGE,"E251"),sQuery(id+"F0.wireOp",EDGE,"E252"),sQuery(id+"F0.wireOp",EDGE,"E253"),sQuery(id+"F0.wireOp",EDGE,"E254"),sQuery(id+"F0.wireOp",EDGE,"E255"),sQuery(id+"F0.wireOp",EDGE,"E256"),sQuery(id+"F0.wireOp",EDGE,"E257"),sQuery(id+"F0.wireOp",EDGE,"E258"),sQuery(id+"F0.wireOp",EDGE,"E259"),sQuery(id+"F0.wireOp",EDGE,"E260"),sQuery(id+"F0.wireOp",EDGE,"E261"),sQuery(id+"F0.wireOp",EDGE,"E262")])],"isStart":false});
            var sketch = newSketch(context, id + "F6", { "sketchPlane" : qUnion([Q0])});
            skLineSegment(sketch, "E519.0", {"start": v(8.05, -12.29) * mm, "end": v(9.58, -11.01) * mm});
            skLineSegment(sketch, "E519.1", {"start": v(4.8, -13.71) * mm, "end": v(8.05, -12.29) * mm});
            skLineSegment(sketch, "E519.2", {"start": v(6.27, 12.3) * mm, "end": v(5.76, 9.43) * mm});
            skLineSegment(sketch, "E519.3", {"start": v(6.89, 13.37) * mm, "end": v(6.27, 12.3) * mm});
            skLineSegment(sketch, "E519.4", {"start": v(7.84, 14.16) * mm, "end": v(6.89, 13.37) * mm});
            skLineSegment(sketch, "E519.5", {"start": v(9, 14.57) * mm, "end": v(7.84, 14.16) * mm});
            skLineSegment(sketch, "E519.6", {"start": v(13.49, 15.27) * mm, "end": v(9, 14.57) * mm});
            skLineSegment(sketch, "E519.7", {"start": v(13.61, 15.27) * mm, "end": v(13.49, 15.27) * mm});
            skLineSegment(sketch, "E519.8", {"start": v(14.03, 15.3) * mm, "end": v(13.61, 15.27) * mm});
            skLineSegment(sketch, "E519.9", {"start": v(15.23, 15.08) * mm, "end": v(14.03, 15.3) * mm});
            skLineSegment(sketch, "E519.10", {"start": v(16.2, 14.53) * mm, "end": v(15.23, 15.08) * mm});
            skLineSegment(sketch, "E519.11", {"start": v(16.37, 14.53) * mm, "end": v(16.2, 14.53) * mm});
            skLineSegment(sketch, "E519.12", {"start": v(19.3, 10.57) * mm, "end": v(16.37, 14.53) * mm});
            skLineSegment(sketch, "E519.13", {"start": v(21.96, 12.73) * mm, "end": v(19.3, 10.57) * mm});
            skLineSegment(sketch, "E519.14", {"start": v(23.13, 13.14) * mm, "end": v(21.96, 12.73) * mm});
            skLineSegment(sketch, "E519.15", {"start": v(27.54, 13.83) * mm, "end": v(23.13, 13.14) * mm});
            skLineSegment(sketch, "E519.16", {"start": v(28.1, 13.87) * mm, "end": v(27.54, 13.83) * mm});
            skLineSegment(sketch, "E519.17", {"start": v(29.33, 13.64) * mm, "end": v(28.1, 13.87) * mm});
            skLineSegment(sketch, "E519.18", {"start": v(30.42, 13) * mm, "end": v(29.33, 13.64) * mm});
            skLineSegment(sketch, "E519.19", {"start": v(31.33, 11.8) * mm, "end": v(30.42, 13) * mm});
            skLineSegment(sketch, "E519.20", {"start": v(31.73, 9.98) * mm, "end": v(31.33, 11.8) * mm});
            skLineSegment(sketch, "E519.21", {"start": v(32.78, 9.48) * mm, "end": v(31.73, 9.98) * mm});
            skLineSegment(sketch, "E519.22", {"start": v(33.79, 8.23) * mm, "end": v(32.78, 9.48) * mm});
            skLineSegment(sketch, "E519.23", {"start": v(34.14, 6.72) * mm, "end": v(33.79, 8.23) * mm});
            skLineSegment(sketch, "E519.24", {"start": v(34.1, 1.67) * mm, "end": v(34.14, 6.72) * mm});
            skLineSegment(sketch, "E519.25", {"start": v(37.12, 1.37) * mm, "end": v(34.1, 1.67) * mm});
            skLineSegment(sketch, "E519.26", {"start": v(38.16, 1.04) * mm, "end": v(37.12, 1.37) * mm});
            skLineSegment(sketch, "E519.27", {"start": v(39.11, 0.53) * mm, "end": v(38.16, 1.04) * mm});
            skLineSegment(sketch, "E519.28", {"start": v(39.94, -0.15) * mm, "end": v(39.11, 0.53) * mm});
            skLineSegment(sketch, "E519.29", {"start": v(40.63, -0.98) * mm, "end": v(39.94, -0.15) * mm});
            skLineSegment(sketch, "E519.30", {"start": v(41.15, -1.93) * mm, "end": v(40.63, -0.98) * mm});
            skLineSegment(sketch, "E519.31", {"start": v(41.47, -2.98) * mm, "end": v(41.15, -1.93) * mm});
            skLineSegment(sketch, "E519.32", {"start": v(10.56, -9.7) * mm, "end": v(14.08, -9.7) * mm});
            skLineSegment(sketch, "E519.33", {"start": v(14.08, -9.7) * mm, "end": v(15.28, -9.45) * mm});
            skLineSegment(sketch, "E519.34", {"start": v(15.28, -9.45) * mm, "end": v(16.48, -9.7) * mm});
            skLineSegment(sketch, "E519.35", {"start": v(16.48, -9.7) * mm, "end": v(20.98, -9.7) * mm});
            skLineSegment(sketch, "E519.36", {"start": v(20.98, -9.7) * mm, "end": v(22.32, -9.42) * mm});
            skLineSegment(sketch, "E519.37", {"start": v(22.32, -9.42) * mm, "end": v(23.7, -8.5) * mm});
            skLineSegment(sketch, "E519.38", {"start": v(23.7, -8.5) * mm, "end": v(25.04, -9.3) * mm});
            skLineSegment(sketch, "E519.39", {"start": v(25.04, -9.3) * mm, "end": v(28.53, -9.83) * mm});
            skLineSegment(sketch, "E519.40", {"start": v(28.53, -9.83) * mm, "end": v(30.4, -9.71) * mm});
            skLineSegment(sketch, "E519.41", {"start": v(30.4, -9.71) * mm, "end": v(32.2, -9.31) * mm});
            skLineSegment(sketch, "E519.42", {"start": v(32.2, -9.31) * mm, "end": v(32.87, -8.96) * mm});
            skLineSegment(sketch, "E519.43", {"start": v(32.87, -8.96) * mm, "end": v(34.87, -9.58) * mm});
            skLineSegment(sketch, "E519.44", {"start": v(34.87, -9.58) * mm, "end": v(36, -9.7) * mm});
            skLineSegment(sketch, "E519.45", {"start": v(36, -9.7) * mm, "end": v(37.13, -9.58) * mm});
            skLineSegment(sketch, "E519.46", {"start": v(37.13, -9.58) * mm, "end": v(38.18, -9.26) * mm});
            skLineSegment(sketch, "E519.47", {"start": v(38.18, -9.26) * mm, "end": v(39.12, -8.74) * mm});
            skLineSegment(sketch, "E519.48", {"start": v(39.12, -8.74) * mm, "end": v(39.95, -8.06) * mm});
            skLineSegment(sketch, "E519.49", {"start": v(39.95, -8.06) * mm, "end": v(40.63, -7.23) * mm});
            skLineSegment(sketch, "E519.50", {"start": v(40.63, -7.23) * mm, "end": v(41.15, -6.28) * mm});
            skLineSegment(sketch, "E519.51", {"start": v(41.15, -6.28) * mm, "end": v(41.47, -5.23) * mm});
            skLineSegment(sketch, "E519.52", {"start": v(41.47, -5.23) * mm, "end": v(41.59, -4.1) * mm});
            skLineSegment(sketch, "E519.53", {"start": v(41.59, -4.1) * mm, "end": v(41.47, -2.98) * mm});
            skLineSegment(sketch, "E519.54", {"start": v(5.76, 9.43) * mm, "end": v(1.04, 9.9) * mm});
            skLineSegment(sketch, "E519.55", {"start": v(9.58, -11.01) * mm, "end": v(10.56, -9.7) * mm});
            skLineSegment(sketch, "E519.56", {"start": v(1.04, 9.9) * mm, "end": v(-2.05, 9.38) * mm});
            skLineSegment(sketch, "E519.57", {"start": v(-2.05, 9.38) * mm, "end": v(-2.83, 11.98) * mm});
            skLineSegment(sketch, "E519.58", {"start": v(-2.83, 11.98) * mm, "end": v(-3.37, 12.98) * mm});
            skLineSegment(sketch, "E519.59", {"start": v(-3.37, 12.98) * mm, "end": v(-4.1, 13.85) * mm});
            skLineSegment(sketch, "E519.60", {"start": v(-4.1, 13.85) * mm, "end": v(-4.98, 14.55) * mm});
            skLineSegment(sketch, "E519.61", {"start": v(-4.98, 14.55) * mm, "end": v(-6, 15.08) * mm});
            skLineSegment(sketch, "E519.62", {"start": v(-6, 15.08) * mm, "end": v(-7.15, 15.4) * mm});
            skLineSegment(sketch, "E519.63", {"start": v(-7.15, 15.4) * mm, "end": v(-8.39, 15.52) * mm});
            skLineSegment(sketch, "E519.64", {"start": v(-8.39, 15.52) * mm, "end": v(-9.62, 15.4) * mm});
            skLineSegment(sketch, "E519.65", {"start": v(-9.62, 15.4) * mm, "end": v(-10.76, 15.08) * mm});
            skLineSegment(sketch, "E519.66", {"start": v(-10.76, 15.08) * mm, "end": v(-11.78, 14.55) * mm});
            skLineSegment(sketch, "E519.67", {"start": v(-11.78, 14.55) * mm, "end": v(-12.67, 13.84) * mm});
            skLineSegment(sketch, "E519.68", {"start": v(-12.67, 13.84) * mm, "end": v(-13.4, 12.98) * mm});
            skLineSegment(sketch, "E519.69", {"start": v(-13.4, 12.98) * mm, "end": v(-13.93, 11.98) * mm});
            skLineSegment(sketch, "E519.70", {"start": v(-13.93, 11.98) * mm, "end": v(-14.5, 10.08) * mm});
            skLineSegment(sketch, "E519.71", {"start": v(-14.5, 10.08) * mm, "end": v(-17.66, 9.78) * mm});
            skLineSegment(sketch, "E519.72", {"start": v(-17.66, 9.78) * mm, "end": v(-18.83, 9.43) * mm});
            skLineSegment(sketch, "E519.73", {"start": v(-18.83, 9.43) * mm, "end": v(-20.04, 9.67) * mm});
            skLineSegment(sketch, "E519.74", {"start": v(-20.04, 9.67) * mm, "end": v(-23.46, 9.67) * mm});
            skLineSegment(sketch, "E519.75", {"start": v(-23.46, 9.67) * mm, "end": v(-25.41, 12.31) * mm});
            skLineSegment(sketch, "E519.76", {"start": v(-25.41, 12.31) * mm, "end": v(-28.31, 13.88) * mm});
            skLineSegment(sketch, "E519.77", {"start": v(-28.31, 13.88) * mm, "end": v(-31.91, 14.42) * mm});
            skLineSegment(sketch, "E519.78", {"start": v(-31.91, 14.42) * mm, "end": v(-35.92, 13.9) * mm});
            skLineSegment(sketch, "E519.79", {"start": v(-35.92, 13.9) * mm, "end": v(-39.55, 12.35) * mm});
            skLineSegment(sketch, "E519.80", {"start": v(-39.55, 12.35) * mm, "end": v(-40.35, 11.68) * mm});
            skLineSegment(sketch, "E519.81", {"start": v(-40.35, 11.68) * mm, "end": v(-40.91, 10.83) * mm});
            skLineSegment(sketch, "E519.82", {"start": v(-40.91, 10.83) * mm, "end": v(-41.2, 9.86) * mm});
            skLineSegment(sketch, "E519.83", {"start": v(-41.2, 9.86) * mm, "end": v(-41.2, 8.86) * mm});
            skLineSegment(sketch, "E519.84", {"start": v(-41.2, 8.86) * mm, "end": v(-40.62, 4.77) * mm});
            skLineSegment(sketch, "E519.85", {"start": v(-40.62, 4.77) * mm, "end": v(-40.62, 4.7) * mm});
            skLineSegment(sketch, "E519.86", {"start": v(-40.62, 4.7) * mm, "end": v(-40.37, 3.83) * mm});
            skLineSegment(sketch, "E519.87", {"start": v(-40.37, 3.83) * mm, "end": v(-38.97, 1.43) * mm});
            skLineSegment(sketch, "E519.88", {"start": v(-38.97, 1.43) * mm, "end": v(-40.56, -0.13) * mm});
            skLineSegment(sketch, "E519.89", {"start": v(-40.56, -0.13) * mm, "end": v(-41.32, -1.27) * mm});
            skLineSegment(sketch, "E519.90", {"start": v(-41.32, -1.27) * mm, "end": v(-41.59, -2.6) * mm});
            skLineSegment(sketch, "E519.91", {"start": v(-41.59, -2.6) * mm, "end": v(-41.59, -6.16) * mm});
            skLineSegment(sketch, "E519.92", {"start": v(-41.59, -6.16) * mm, "end": v(-41.32, -7.5) * mm});
            skLineSegment(sketch, "E519.93", {"start": v(-41.32, -7.5) * mm, "end": v(-40.55, -8.65) * mm});
            skLineSegment(sketch, "E519.94", {"start": v(-40.55, -8.65) * mm, "end": v(-39.41, -9.42) * mm});
            skLineSegment(sketch, "E519.95", {"start": v(-39.41, -9.42) * mm, "end": v(-38.05, -9.7) * mm});
            skLineSegment(sketch, "E519.96", {"start": v(-38.05, -9.7) * mm, "end": v(-25.2, -9.7) * mm});
            skLineSegment(sketch, "E519.97", {"start": v(-25.2, -9.7) * mm, "end": v(-24.74, -9.59) * mm});
            skLineSegment(sketch, "E519.98", {"start": v(-24.74, -9.59) * mm, "end": v(-24.07, -9.72) * mm});
            skLineSegment(sketch, "E519.99", {"start": v(-24.07, -9.72) * mm, "end": v(-19.57, -9.72) * mm});
            skLineSegment(sketch, "E519.100", {"start": v(-19.57, -9.72) * mm, "end": v(-18.37, -9.48) * mm});
            skLineSegment(sketch, "E519.101", {"start": v(-18.37, -9.48) * mm, "end": v(-17.17, -9.72) * mm});
            skLineSegment(sketch, "E519.102", {"start": v(-17.17, -9.72) * mm, "end": v(-12.68, -9.72) * mm});
            skLineSegment(sketch, "E519.103", {"start": v(-12.68, -9.72) * mm, "end": v(-11.65, -9.52) * mm});
            skLineSegment(sketch, "E519.104", {"start": v(-11.65, -9.52) * mm, "end": v(-10.63, -9.72) * mm});
            skLineSegment(sketch, "E519.105", {"start": v(-10.63, -9.72) * mm, "end": v(-8.78, -9.72) * mm});
            skLineSegment(sketch, "E519.106", {"start": v(-8.78, -9.72) * mm, "end": v(-6.58, -12.08) * mm});
            skLineSegment(sketch, "E519.107", {"start": v(-6.58, -12.08) * mm, "end": v(-5.05, -13.05) * mm});
            skLineSegment(sketch, "E519.108", {"start": v(-5.05, -13.05) * mm, "end": v(-2.38, -13.91) * mm});
            skLineSegment(sketch, "E519.109", {"start": v(-2.38, -13.91) * mm, "end": v(0.9, -14.2) * mm});
            skLineSegment(sketch, "E519.110", {"start": v(0.9, -14.2) * mm, "end": v(4.8, -13.71) * mm});
            skSolve(sketch);
        }
        {
            var Q0;
            Q0=makeQuery(id+"F6.imprint","IMPRINT",FACE,{"disambiguationData":[TD([[makeQuery(id+"F6.imprint","IMPRINT",EDGE,{"derivedFrom":sQuery(id+"F6.wireOp",EDGE,"E519.0")}),1.0]])]});
            extrude(context, id + "F7", {"entities" : qUnion([Q0]), "oppositeDirection" : true, "depth" : 15 * mm});
        }
        {
            var Q0;
            Q0=makeQuery(id+"F5.opExtrude","CAP_FACE",FACE,{"disambiguationData":[OSD([sQuery(id+"F0.wireOp",EDGE,"E0"),sQuery(id+"F0.wireOp",EDGE,"E1"),sQuery(id+"F0.wireOp",EDGE,"E2"),sQuery(id+"F0.wireOp",EDGE,"E3"),sQuery(id+"F0.wireOp",EDGE,"E4"),sQuery(id+"F0.wireOp",EDGE,"E5"),sQuery(id+"F0.wireOp",EDGE,"E6"),sQuery(id+"F0.wireOp",EDGE,"E7"),sQuery(id+"F0.wireOp",EDGE,"E8"),sQuery(id+"F0.wireOp",EDGE,"E9"),sQuery(id+"F0.wireOp",EDGE,"E10"),sQuery(id+"F0.wireOp",EDGE,"E11"),sQuery(id+"F0.wireOp",EDGE,"E12"),sQuery(id+"F0.wireOp",EDGE,"E13"),sQuery(id+"F0.wireOp",EDGE,"E14"),sQuery(id+"F0.wireOp",EDGE,"E15"),sQuery(id+"F0.wireOp",EDGE,"E16"),sQuery(id+"F0.wireOp",EDGE,"E17"),sQuery(id+"F0.wireOp",EDGE,"E18"),sQuery(id+"F0.wireOp",EDGE,"E19"),sQuery(id+"F0.wireOp",EDGE,"E20"),sQuery(id+"F0.wireOp",EDGE,"E21"),sQuery(id+"F0.wireOp",EDGE,"E22"),sQuery(id+"F0.wireOp",EDGE,"E34"),sQuery(id+"F0.wireOp",EDGE,"E35"),sQuery(id+"F0.wireOp",EDGE,"E36"),sQuery(id+"F0.wireOp",EDGE,"E37"),sQuery(id+"F0.wireOp",EDGE,"E38"),sQuery(id+"F0.wireOp",EDGE,"E39"),sQuery(id+"F0.wireOp",EDGE,"E40"),sQuery(id+"F0.wireOp",EDGE,"E41"),sQuery(id+"F0.wireOp",EDGE,"E50"),sQuery(id+"F0.wireOp",EDGE,"E51"),sQuery(id+"F0.wireOp",EDGE,"E52"),sQuery(id+"F0.wireOp",EDGE,"E53"),sQuery(id+"F0.wireOp",EDGE,"E54"),sQuery(id+"F0.wireOp",EDGE,"E55"),sQuery(id+"F0.wireOp",EDGE,"E63"),sQuery(id+"F0.wireOp",EDGE,"E64"),sQuery(id+"F0.wireOp",EDGE,"E65"),sQuery(id+"F0.wireOp",EDGE,"E66"),sQuery(id+"F0.wireOp",EDGE,"E67"),sQuery(id+"F0.wireOp",EDGE,"E68"),sQuery(id+"F0.wireOp",EDGE,"E69"),sQuery(id+"F0.wireOp",EDGE,"E70"),sQuery(id+"F0.wireOp",EDGE,"E71"),sQuery(id+"F0.wireOp",EDGE,"E72"),sQuery(id+"F0.wireOp",EDGE,"E87"),sQuery(id+"F0.wireOp",EDGE,"E88"),sQuery(id+"F0.wireOp",EDGE,"E89"),sQuery(id+"F0.wireOp",EDGE,"E90"),sQuery(id+"F0.wireOp",EDGE,"E91"),sQuery(id+"F0.wireOp",EDGE,"E92"),sQuery(id+"F0.wireOp",EDGE,"E93"),sQuery(id+"F0.wireOp",EDGE,"E94"),sQuery(id+"F0.wireOp",EDGE,"E95"),sQuery(id+"F0.wireOp",EDGE,"E105"),sQuery(id+"F0.wireOp",EDGE,"E106"),sQuery(id+"F0.wireOp",EDGE,"E117"),sQuery(id+"F0.wireOp",EDGE,"E118"),sQuery(id+"F0.wireOp",EDGE,"E119"),sQuery(id+"F0.wireOp",EDGE,"E120"),sQuery(id+"F0.wireOp",EDGE,"E121"),sQuery(id+"F0.wireOp",EDGE,"E132"),sQuery(id+"F0.wireOp",EDGE,"E133"),sQuery(id+"F0.wireOp",EDGE,"E134"),sQuery(id+"F0.wireOp",EDGE,"E135"),sQuery(id+"F0.wireOp",EDGE,"E136"),sQuery(id+"F0.wireOp",EDGE,"E137"),sQuery(id+"F0.wireOp",EDGE,"E138"),sQuery(id+"F0.wireOp",EDGE,"E139"),sQuery(id+"F0.wireOp",EDGE,"E140"),sQuery(id+"F0.wireOp",EDGE,"E141"),sQuery(id+"F0.wireOp",EDGE,"E157"),sQuery(id+"F0.wireOp",EDGE,"E158"),sQuery(id+"F0.wireOp",EDGE,"E159"),sQuery(id+"F0.wireOp",EDGE,"E160"),sQuery(id+"F0.wireOp",EDGE,"E161"),sQuery(id+"F0.wireOp",EDGE,"E162"),sQuery(id+"F0.wireOp",EDGE,"E163"),sQuery(id+"F0.wireOp",EDGE,"E164"),sQuery(id+"F0.wireOp",EDGE,"E169"),sQuery(id+"F0.wireOp",EDGE,"E170"),sQuery(id+"F0.wireOp",EDGE,"E171"),sQuery(id+"F0.wireOp",EDGE,"E172"),sQuery(id+"F0.wireOp",EDGE,"E173"),sQuery(id+"F0.wireOp",EDGE,"E174"),sQuery(id+"F0.wireOp",EDGE,"E175"),sQuery(id+"F0.wireOp",EDGE,"E180"),sQuery(id+"F0.wireOp",EDGE,"E181"),sQuery(id+"F0.wireOp",EDGE,"E182"),sQuery(id+"F0.wireOp",EDGE,"E183"),sQuery(id+"F0.wireOp",EDGE,"E184"),sQuery(id+"F0.wireOp",EDGE,"E185"),sQuery(id+"F0.wireOp",EDGE,"E186"),sQuery(id+"F0.wireOp",EDGE,"E187"),sQuery(id+"F0.wireOp",EDGE,"E188"),sQuery(id+"F0.wireOp",EDGE,"E189"),sQuery(id+"F0.wireOp",EDGE,"E190"),sQuery(id+"F0.wireOp",EDGE,"E191"),sQuery(id+"F0.wireOp",EDGE,"E192"),sQuery(id+"F0.wireOp",EDGE,"E193"),sQuery(id+"F0.wireOp",EDGE,"E194"),sQuery(id+"F0.wireOp",EDGE,"E195"),sQuery(id+"F0.wireOp",EDGE,"E196"),sQuery(id+"F0.wireOp",EDGE,"E209"),sQuery(id+"F0.wireOp",EDGE,"E210"),sQuery(id+"F0.wireOp",EDGE,"E211"),sQuery(id+"F0.wireOp",EDGE,"E212"),sQuery(id+"F0.wireOp",EDGE,"E213"),sQuery(id+"F0.wireOp",EDGE,"E219"),sQuery(id+"F0.wireOp",EDGE,"E220"),sQuery(id+"F0.wireOp",EDGE,"E221"),sQuery(id+"F0.wireOp",EDGE,"E222"),sQuery(id+"F0.wireOp",EDGE,"E223"),sQuery(id+"F0.wireOp",EDGE,"E224"),sQuery(id+"F0.wireOp",EDGE,"E225"),sQuery(id+"F0.wireOp",EDGE,"E226"),sQuery(id+"F0.wireOp",EDGE,"E227"),sQuery(id+"F0.wireOp",EDGE,"E228"),sQuery(id+"F0.wireOp",EDGE,"E229"),sQuery(id+"F0.wireOp",EDGE,"E230"),sQuery(id+"F0.wireOp",EDGE,"E231"),sQuery(id+"F0.wireOp",EDGE,"E232"),sQuery(id+"F0.wireOp",EDGE,"E233"),sQuery(id+"F0.wireOp",EDGE,"E234"),sQuery(id+"F0.wireOp",EDGE,"E243"),sQuery(id+"F0.wireOp",EDGE,"E244"),sQuery(id+"F0.wireOp",EDGE,"E245"),sQuery(id+"F0.wireOp",EDGE,"E246"),sQuery(id+"F0.wireOp",EDGE,"E247"),sQuery(id+"F0.wireOp",EDGE,"E248"),sQuery(id+"F0.wireOp",EDGE,"E249"),sQuery(id+"F0.wireOp",EDGE,"E250"),sQuery(id+"F0.wireOp",EDGE,"E251"),sQuery(id+"F0.wireOp",EDGE,"E252"),sQuery(id+"F0.wireOp",EDGE,"E253"),sQuery(id+"F0.wireOp",EDGE,"E254"),sQuery(id+"F0.wireOp",EDGE,"E255"),sQuery(id+"F0.wireOp",EDGE,"E256"),sQuery(id+"F0.wireOp",EDGE,"E257"),sQuery(id+"F0.wireOp",EDGE,"E258"),sQuery(id+"F0.wireOp",EDGE,"E259"),sQuery(id+"F0.wireOp",EDGE,"E260"),sQuery(id+"F0.wireOp",EDGE,"E261"),sQuery(id+"F0.wireOp",EDGE,"E262")])],"isStart":false});
            var sketch = newSketch(context, id + "F8", { "sketchPlane" : qUnion([Q0])});
            skLineSegment(sketch, "E520", {"start": v(-40.22, 4.8) * mm, "end": v(-46.98, 4.8) * mm});
            skLineSegment(sketch, "E521", {"start": v(-46.98, 4.8) * mm, "end": v(-46.98, -3.59) * mm});
            skLineSegment(sketch, "E522", {"start": v(-46.98, -3.59) * mm, "end": v(-41.19, -3.59) * mm});
            skLineSegment(sketch, "E523", {"start": v(33.71, 4.8) * mm, "end": v(40.47, 4.8) * mm});
            skLineSegment(sketch, "E524", {"start": v(40.47, 4.8) * mm, "end": v(40.3, -1.2) * mm});
            skSolve(sketch);
        }
        {
            var Q0;
            {var subQ4=sQuery(id+"F8.wireOp",EDGE,"E524");Q0=makeQuery(id+"F8.imprint","IMPRINT",FACE,{"disambiguationData":[TD([[makeQuery(id+"F8.imprint","IMPRINT",EDGE,{"derivedFrom":subQ4}),-1.0]])]});}
            var Q1;
            Q1=makeQuery(id+"F8.imprint","IMPRINT",FACE,{"disambiguationData":[TD([[makeQuery(id+"F8.imprint","IMPRINT",EDGE,{"derivedFrom":sQuery(id+"F8.wireOp",EDGE,"E520")}),1.0]])]});
            extrude(context, id + "F9", {"entities" : qUnion([Q0, Q1]), "operationType" : NewBodyOperationType.ADD, "oppositeDirection" : true, "depth" : 6 * mm});
        }
        {
            var Q0;
            Q0=makeQuery(id+"F6.imprint","IMPRINT",FACE,{"disambiguationData":[TD([[makeQuery(id+"F6.imprint","IMPRINT",EDGE,{"derivedFrom":makeQuery(id+"F5.opExtrude","CAP_EDGE",EDGE,{"disambiguationData":[OSD([sQuery(id+"F0.wireOp",EDGE,"E0")])],"isStart":false})}),1.0]])]});
            var Q1;
            Q1=makeQuery(id+"F6.imprint","IMPRINT",FACE,{"disambiguationData":[TD([[makeQuery(id+"F6.imprint","IMPRINT",EDGE,{"derivedFrom":sQuery(id+"F6.wireOp",EDGE,"E519.0")}),1.0]])]});
            extrude(context, id + "F10", {"entities" : qUnion([Q0, Q1]), "operationType" : NewBodyOperationType.ADD, "oppositeDirection" : true, "depth" : 1 * mm});
        }
    });
